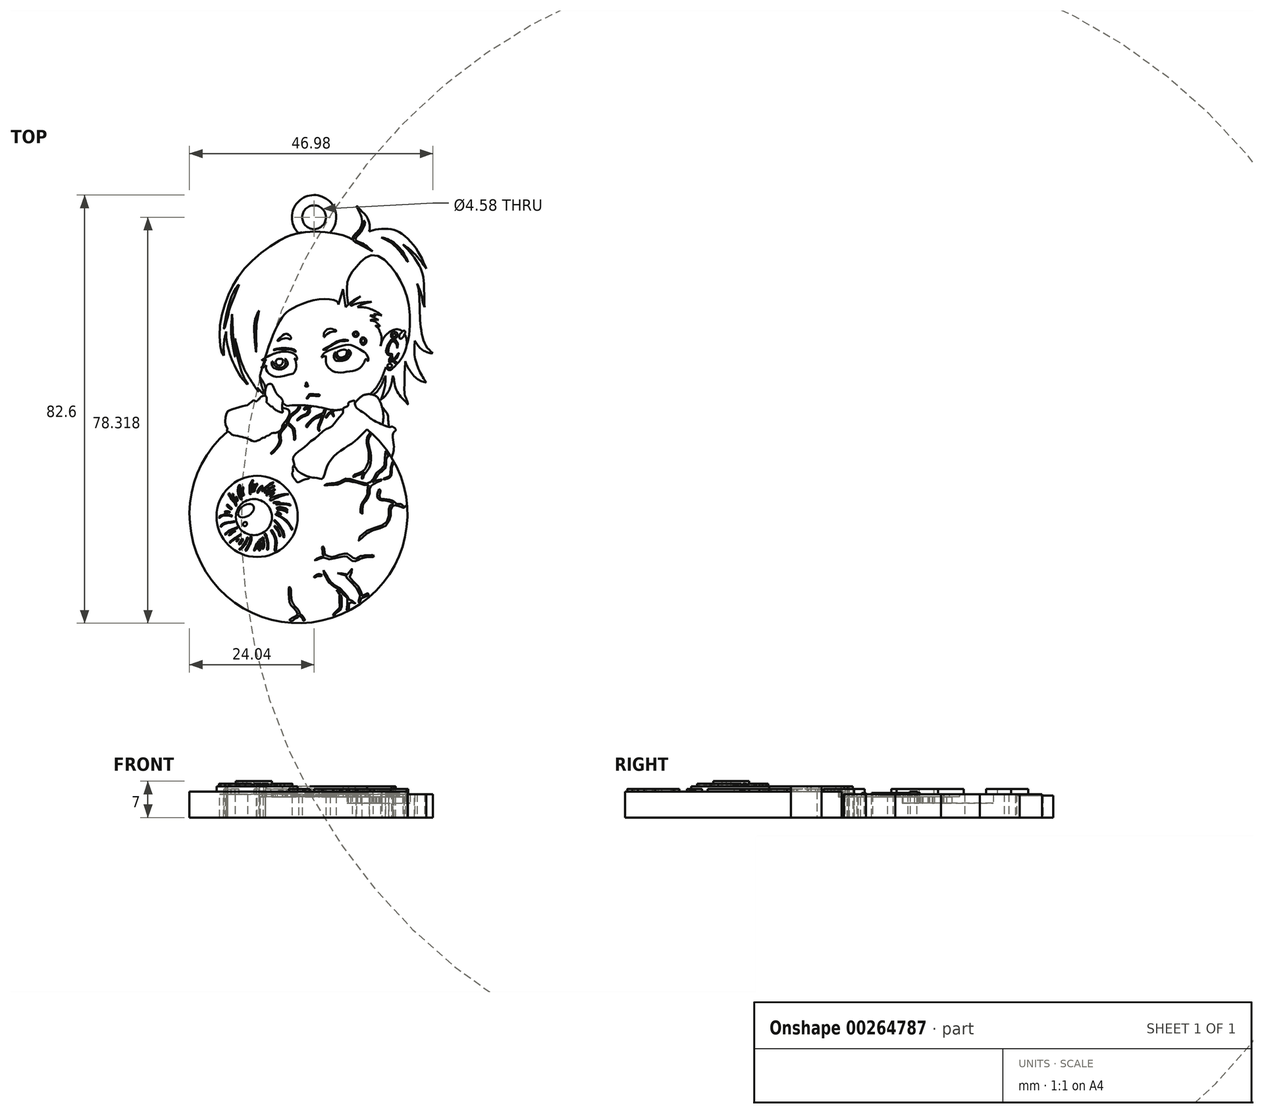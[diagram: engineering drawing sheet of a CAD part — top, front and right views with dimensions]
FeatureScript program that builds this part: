
annotation { "Feature Type Name" : "Feature", "Feature Type Description" : "" }
export const myFeature = defineFeature(function(context is Context, id is Id, definition is map)
    precondition{}
    {
        {
            var Q0;
            Q0=qCreatedBy(makeId("Top.planeOp"),FACE);
            var sketch = newSketch(context, id + "F0", { "sketchPlane" : qUnion([Q0])});
            skLineSegment(sketch, "E0", {"start": v(0, -34.76) * mm, "end": v(0, 40.24) * mm, "construction": true});
            skCircle(sketch, "E1", {"center": v(-3, -13.34) * mm, "radius": 21.03 * mm});
            skCircle(sketch, "E2", {"center": v(-10.98, -13.78) * mm, "radius": 7.83 * mm});
            skCircle(sketch, "E3", {"center": v(-11.61, -13.92) * mm, "radius": 3.48 * mm});
            skEllipse(sketch, "E4", {"center": v(-13.11, -12.67) * mm, "majorRadius": 1.7 * mm, "minorRadius": 1.07 * mm, "majorAxis": v(0.82, 0.58)});
            skEllipse(sketch, "E5", {"center": v(-13.33, -15.26) * mm, "majorRadius": 0.42 * mm, "minorRadius": 0.37 * mm, "majorAxis": v(0.66, 0.75)});
            skFitSpline(sketch, "E6", {"points": [v(5.58, 30.11) * mm, v(4.68, 27.12) * mm], "startDerivative": vector(-0.9, -3) * mm, "endDerivative": vector(-0.9, -3) * mm});
            skFitSpline(sketch, "E7", {"points": [v(4.68, 27.12) * mm, v(4.48, 27.66) * mm, v(0.94, 28.09) * mm, v(-4.3, 26.3) * mm, v(-6.06, 24.76) * mm, v(-8.26, 20.35) * mm, v(-10.45, 13.34) * mm], "startDerivative": vector(-0.38, 8.67) * mm, "endDerivative": vector(-8.55, -30.7) * mm});
            skFitSpline(sketch, "E8", {"points": [v(-10.45, 13.34) * mm, v(-9.57, 10.69) * mm, v(-5.18, 7.57) * mm, v(-5.04, 7.59) * mm], "startDerivative": vector(0.18, -6.54) * mm, "endDerivative": vector(0.96, 0.67) * mm, "construction": true});
            skFitSpline(sketch, "E9", {"points": [v(5.58, 30.11) * mm, v(6.1, 26.6) * mm], "startDerivative": vector(0.52, -3.51) * mm, "endDerivative": vector(0.52, -3.51) * mm});
            skFitSpline(sketch, "E10", {"points": [v(6.1, 26.6) * mm, v(7.25, 27.65) * mm, v(8.97, 28.67) * mm], "startDerivative": vector(2.26, 2.3) * mm, "endDerivative": vector(3.45, 1.84) * mm});
            skFitSpline(sketch, "E11", {"points": [v(8.97, 28.67) * mm, v(7.37, 27.4) * mm, v(7.02, 26.82) * mm], "startDerivative": vector(-3, -2.14) * mm, "endDerivative": vector(-0.67, -1.5) * mm});
            skFitSpline(sketch, "E12", {"points": [v(7.02, 26.82) * mm, v(8.36, 27.32) * mm, v(11.11, 27.65) * mm], "startDerivative": vector(2.88, 1.33) * mm, "endDerivative": vector(5.18, 0.37) * mm});
            skFitSpline(sketch, "E13", {"points": [v(11.11, 27.65) * mm, v(9.22, 27.12) * mm, v(8.36, 26.6) * mm], "startDerivative": vector(-3.6, -0.8) * mm, "endDerivative": vector(-1.81, -1.33) * mm});
            skFitSpline(sketch, "E14", {"points": [v(8.36, 26.6) * mm, v(10.24, 26.46) * mm, v(12.26, 25.6) * mm, v(13.1, 25) * mm], "startDerivative": vector(5.16, 0.08) * mm, "endDerivative": vector(2.75, -2.21) * mm});
            skFitSpline(sketch, "E15", {"points": [v(13.1, 25) * mm, v(12.29, 25.18) * mm, v(11.49, 25.26) * mm], "startDerivative": vector(-1.61, 0.44) * mm, "endDerivative": vector(-1.62, 0.1) * mm});
            skFitSpline(sketch, "E16", {"points": [v(11.49, 25.26) * mm, v(11.84, 24.84) * mm], "startDerivative": vector(0.36, -0.42) * mm, "endDerivative": vector(0.36, -0.42) * mm});
            skFitSpline(sketch, "E17", {"points": [v(11.84, 24.84) * mm, v(11.32, 24.98) * mm, v(10.77, 24.98) * mm], "startDerivative": vector(-1.03, 0.35) * mm, "endDerivative": vector(-1.1, -0.07) * mm});
            skFitSpline(sketch, "E18", {"points": [v(10.77, 24.98) * mm, v(11.49, 24.63) * mm, v(12.05, 24.34) * mm], "startDerivative": vector(1.4, -0.66) * mm, "endDerivative": vector(1.15, -0.62) * mm});
            skFitSpline(sketch, "E19", {"points": [v(12.05, 24.2) * mm, v(11.11, 24.18) * mm, v(10.77, 24.03) * mm], "startDerivative": vector(-1.72, 0.09) * mm, "endDerivative": vector(-0.75, -0.45) * mm});
            skFitSpline(sketch, "E20", {"points": [v(10.77, 24.03) * mm, v(11.72, 23.85) * mm, v(12.73, 22.94) * mm], "startDerivative": vector(2.12, -0.1) * mm, "endDerivative": vector(1.8, -2.01) * mm});
            skFitSpline(sketch, "E21", {"points": [v(12.73, 22.94) * mm, v(12.27, 22.94) * mm, v(11.84, 23.08) * mm], "startDerivative": vector(-0.93, -0.07) * mm, "endDerivative": vector(-0.85, 0.33) * mm});
            skFitSpline(sketch, "E22", {"points": [v(11.84, 23.08) * mm, v(12.05, 22.81) * mm, v(12.43, 22.56) * mm], "startDerivative": vector(0.39, -0.6) * mm, "endDerivative": vector(0.79, -0.44) * mm});
            skFitSpline(sketch, "E23", {"points": [v(12.43, 22.56) * mm, v(12.73, 21.82) * mm, v(13.03, 20.69) * mm, v(12.8, 19.08) * mm], "startDerivative": vector(1.04, -2.57) * mm, "endDerivative": vector(-1, -4.25) * mm});
            skFitSpline(sketch, "E24", {"points": [v(12.8, 19.08) * mm, v(13.4, 20.6) * mm, v(14.78, 21.94) * mm, v(16.64, 22.21) * mm, v(17.85, 20.34) * mm, v(17.08, 17.09) * mm, v(15.2, 14.82) * mm, v(14.61, 14.47) * mm, v(14.16, 14.62) * mm, v(13.86, 15.02) * mm], "startDerivative": vector(3.97, 13.82) * mm, "endDerivative": vector(-4.09, 7.1) * mm});
            skFitSpline(sketch, "E25", {"points": [v(13.86, 15.02) * mm, v(12.73, 12.26) * mm, v(10.77, 9.8) * mm, v(5.58, 6.93) * mm, v(2.97, 6.82) * mm], "startDerivative": vector(-4.59, -12.56) * mm, "endDerivative": vector(-10.9, 1.16) * mm});
            skFitSpline(sketch, "E26", {"points": [v(-10.45, 13.34) * mm, v(-10.16, 11.62) * mm, v(-9.57, 10.69) * mm, v(-5.3, 7.56) * mm], "startDerivative": vector(0.84, -6.71) * mm, "endDerivative": vector(10.7, -7.31) * mm});
            skFitSpline(sketch, "E27", {"points": [v(-5.3, 7.56) * mm, v(-3.07, 7.08) * mm, v(2.97, 6.82) * mm], "startDerivative": vector(5.13, -1.43) * mm, "endDerivative": vector(10.95, -0.15) * mm});
            skFitSpline(sketch, "E28", {"points": [v(12.05, 24.2) * mm, v(12.47, 24.09) * mm], "startDerivative": vector(0.42, -0.1) * mm, "endDerivative": vector(0.42, -0.1) * mm});
            skFitSpline(sketch, "E29", {"points": [v(12.05, 24.34) * mm, v(12.47, 24.09) * mm], "startDerivative": vector(0.42, -0.25) * mm, "endDerivative": vector(0.42, -0.25) * mm});
            skFitSpline(sketch, "E30", {"points": [v(-10.42, 13.07) * mm, v(-10.02, 12.46) * mm, v(-9.54, 11.58) * mm, v(-9.41, 10.76) * mm, v(-9.57, 10.4) * mm], "startDerivative": vector(1.55, -2.28) * mm, "endDerivative": vector(-1.1, -1.74) * mm});
            skFitSpline(sketch, "E31", {"points": [v(-9.57, 10.4) * mm, v(-9.57, 11.1) * mm, v(-10.02, 11.81) * mm, v(-10.26, 12.02) * mm], "startDerivative": vector(0.3, 1.92) * mm, "endDerivative": vector(-0.9, 0.65) * mm});
            skFitSpline(sketch, "E32", {"points": [v(-10.26, 12.02) * mm, v(-10.06, 11.22) * mm, v(-9.8, 10.55) * mm, v(-9.76, 9.84) * mm], "startDerivative": vector(0.48, -2.36) * mm, "endDerivative": vector(-0.04, -2.24) * mm});
            skFitSpline(sketch, "E33", {"points": [v(-9.76, 9.84) * mm, v(-10.26, 10.33) * mm, v(-10.96, 11.05) * mm], "startDerivative": vector(-1.04, 1.02) * mm, "endDerivative": vector(-1.34, 1.38) * mm});
            skFitSpline(sketch, "E34", {"points": [v(-10.96, 11.05) * mm, v(-10.82, 10.69) * mm, v(-10.68, 10.28) * mm], "startDerivative": vector(0.3, -0.72) * mm, "endDerivative": vector(0.25, -0.81) * mm});
            skFitSpline(sketch, "E35", {"points": [v(-10.68, 10.28) * mm, v(-11.1, 10.76) * mm, v(-12.08, 12.3) * mm, v(-13.34, 14.38) * mm, v(-14.31, 16.92) * mm, v(-15, 19.4) * mm, v(-15.26, 20.58) * mm], "startDerivative": vector(-3.85, 4.06) * mm, "endDerivative": vector(-1.7, 7.84) * mm});
            skFitSpline(sketch, "E36", {"points": [v(-15.26, 20.58) * mm, v(-14.82, 17.19) * mm, v(-14.06, 14.43) * mm, v(-13.38, 12.75) * mm, v(-12.93, 12.07) * mm, v(-12.82, 11.68) * mm], "startDerivative": vector(1.14, -12.13) * mm, "endDerivative": vector(0.06, -4.82) * mm});
            skFitSpline(sketch, "E37", {"points": [v(-12.82, 11.68) * mm, v(-13.67, 12.58) * mm, v(-15.47, 15.57) * mm, v(-16.5, 18.41) * mm, v(-16.9, 20.4) * mm, v(-16.95, 21.87) * mm], "startDerivative": vector(-5.16, 4.82) * mm, "endDerivative": vector(0.07, 8.66) * mm});
            skFitSpline(sketch, "E38", {"points": [v(-16.95, 21.87) * mm, v(-17.4, 19.73) * mm, v(-17.4, 17.29) * mm], "startDerivative": vector(-1.13, -4.32) * mm, "endDerivative": vector(0.23, -4.84) * mm});
            skFitSpline(sketch, "E39", {"points": [v(-17.4, 17.29) * mm, v(-17.91, 18.21) * mm, v(-18.13, 23.19) * mm, v(-16.37, 29.33) * mm, v(-13.15, 34.33) * mm, v(-7.4, 39.04) * mm, v(-3, 40.9) * mm, v(2.6, 41.04) * mm, v(6.38, 40.2) * mm, v(7.36, 39.66) * mm], "startDerivative": vector(-10.15, 12.6) * mm, "endDerivative": vector(14.26, -9.35) * mm});
            skFitSpline(sketch, "E40", {"points": [v(6.6, 27.1) * mm, v(6.43, 28.26) * mm, v(6.33, 30.55) * mm, v(6.8, 32.52) * mm, v(8.14, 34.36) * mm, v(9.76, 36.02) * mm, v(12.05, 36.6) * mm, v(15.18, 34.02) * mm, v(17.25, 30.46) * mm, v(18.46, 25.7) * mm, v(18.22, 20.5) * mm, v(17.85, 19.21) * mm], "startDerivative": vector(-3.09, 17.78) * mm, "endDerivative": vector(-6.02, -16.42) * mm});
            skFitSpline(sketch, "E41", {"points": [v(7.36, 39.66) * mm, v(7.63, 40.38) * mm, v(8.53, 41.33) * mm, v(9.18, 42.46) * mm, v(9.2, 43.8) * mm, v(8.45, 45.56) * mm, v(8.17, 45.94) * mm], "startDerivative": vector(1.2, 5.27) * mm, "endDerivative": vector(-2.32, 2.66) * mm});
            skFitSpline(sketch, "E42", {"points": [v(8.17, 45.94) * mm, v(8.17, 46.01) * mm, v(8.26, 46.07) * mm, v(9.14, 45.18) * mm, v(9.84, 44.48) * mm, v(10.47, 43.44) * mm, v(10.76, 42.12) * mm, v(10.62, 41.17) * mm], "startDerivative": vector(-0.3, 1.56) * mm, "endDerivative": vector(-1.33, -5.49) * mm});
            skFitSpline(sketch, "E43", {"points": [v(10.62, 41.17) * mm, v(12.06, 41.61) * mm, v(14.76, 41.64) * mm, v(16.97, 40.74) * mm, v(19.96, 37.49) * mm, v(21.65, 34.02) * mm], "startDerivative": vector(8.87, 3.5) * mm, "endDerivative": vector(6, -14.88) * mm});
            skFitSpline(sketch, "E44", {"points": [v(21.65, 34.02) * mm, v(19.22, 37.07) * mm, v(17.13, 38.73) * mm], "startDerivative": vector(-4.4, 6.1) * mm, "endDerivative": vector(-4.66, 3.22) * mm});
            skFitSpline(sketch, "E45", {"points": [v(17.13, 38.73) * mm, v(18.22, 37.57) * mm, v(19.68, 35.64) * mm, v(20.91, 33.13) * mm, v(21.23, 30.02) * mm, v(21.31, 26.57) * mm], "startDerivative": vector(6.89, -6.9) * mm, "endDerivative": vector(0.35, -15.15) * mm});
            skFitSpline(sketch, "E46", {"points": [v(21.31, 26.57) * mm, v(20.95, 27.65) * mm, v(20.75, 28.94) * mm, v(19.88, 31.15) * mm], "startDerivative": vector(-1.5, 3.74) * mm, "endDerivative": vector(-2.63, 5.69) * mm});
            skFitSpline(sketch, "E47", {"points": [v(19.88, 31.15) * mm, v(20.26, 29.29) * mm, v(20.4, 25.3) * mm, v(20.74, 21.75) * mm, v(21.65, 19.05) * mm, v(22.94, 17.75) * mm], "startDerivative": vector(2.72, -10) * mm, "endDerivative": vector(8.56, -6.83) * mm});
            skFitSpline(sketch, "E48", {"points": [v(22.94, 17.75) * mm, v(22.4, 17.75) * mm, v(20.76, 18.46) * mm, v(19.46, 20.14) * mm], "startDerivative": vector(-2.22, -0.26) * mm, "endDerivative": vector(-2.67, 4.52) * mm});
            skFitSpline(sketch, "E49", {"points": [v(19.46, 20.14) * mm, v(19.46, 16.97) * mm, v(20.52, 13.93) * mm, v(21.65, 12.06) * mm], "startDerivative": vector(-0.74, -8.97) * mm, "endDerivative": vector(3.88, -5.9) * mm});
            skFitSpline(sketch, "E50", {"points": [v(21.65, 12.06) * mm, v(19.88, 12.77) * mm, v(18.19, 14.85) * mm, v(17.6, 16.19) * mm], "startDerivative": vector(-5.45, 1.3) * mm, "endDerivative": vector(-0.83, 4.43) * mm});
            skFitSpline(sketch, "E51", {"points": [v(17.6, 16.19) * mm, v(17.45, 12.06) * mm, v(17.55, 9.48) * mm, v(18.02, 8.37) * mm, v(18.07, 7.84) * mm, v(17.95, 7.99) * mm], "startDerivative": vector(-1.15, -12.43) * mm, "endDerivative": vector(-3.15, 1.58) * mm});
            skFitSpline(sketch, "E52", {"points": [v(17.95, 7.99) * mm, v(17.6, 8.44) * mm, v(17.2, 8.8) * mm, v(15.84, 10.72) * mm, v(15.38, 12.83) * mm, v(15.2, 13.37) * mm], "startDerivative": vector(-1.6, 3.14) * mm, "endDerivative": vector(-1.32, 3.11) * mm});
            skFitSpline(sketch, "E53", {"points": [v(15.2, 13.37) * mm, v(14.75, 11.25) * mm, v(13.9, 9.68) * mm, v(12.81, 8.68) * mm], "startDerivative": vector(-0.97, -5.97) * mm, "endDerivative": vector(-3.83, -2.99) * mm});
            skFitSpline(sketch, "E54", {"points": [v(12.81, 8.68) * mm, v(13.23, 9.64) * mm, v(13.73, 11.8) * mm, v(13.77, 13.37) * mm], "startDerivative": vector(1.53, 3.05) * mm, "endDerivative": vector(-0.14, 4.4) * mm});
            skFitSpline(sketch, "E55", {"points": [v(13.77, 13.37) * mm, v(12.81, 11.27) * mm, v(11.54, 9.8) * mm, v(10.27, 9.4) * mm], "startDerivative": vector(-2.3, -5.76) * mm, "endDerivative": vector(-4.58, -0.8) * mm});
            skFitSpline(sketch, "E56", {"points": [v(-8.58, 11.81) * mm, v(-9.14, 11.44) * mm, v(-9.41, 9.56) * mm, v(-9.2, 9.26) * mm, v(-9.15, 8.51) * mm, v(-9.2, 8.32) * mm, v(-8.74, 7.85) * mm, v(-8.24, 7.4) * mm, v(-8, 7.39) * mm, v(-7.75, 7.03) * mm, v(-6.2, 6.3) * mm, v(-6.01, 6.4) * mm, v(-6.1, 6.72) * mm, v(-6.13, 7.85) * mm, v(-6.03, 8.51) * mm, v(-6.55, 9.27) * mm, v(-7.23, 9.9) * mm, v(-7.74, 10.95) * mm, v(-8.14, 11.7) * mm, v(-8.58, 11.81) * mm]});
            skFitSpline(sketch, "E57", {"points": [v(-9.41, 9.56) * mm, v(-10.1, 9.38) * mm, v(-10.51, 9.06) * mm, v(-10.54, 8.83) * mm], "startDerivative": vector(-1.78, -0.33) * mm, "endDerivative": vector(-0.03, -1.55) * mm});
            skFitSpline(sketch, "E58", {"points": [v(-10.54, 8.83) * mm, v(-10.7, 8.83) * mm, v(-10.93, 8.56) * mm, v(-11.16, 8.4) * mm], "startDerivative": vector(-1.15, 0.03) * mm, "endDerivative": vector(-0.57, -0.65) * mm});
            skFitSpline(sketch, "E59", {"points": [v(-11.16, 8.4) * mm, v(-11.4, 8.53) * mm, v(-11.7, 8.62) * mm, v(-11.94, 8.4) * mm, v(-12.28, 8.15) * mm, v(-12.48, 7.98) * mm, v(-12.8, 7.73) * mm, v(-13.88, 7.45) * mm, v(-16, 6.83) * mm, v(-16.83, 6.28) * mm, v(-17.01, 3.73) * mm, v(-16.71, 3.09) * mm, v(-16.81, 2.73) * mm, v(-16.2, 2.35) * mm, v(-15.96, 2.07) * mm, v(-14.06, 1.61) * mm, v(-12.53, 1.1) * mm, v(-11.43, 0.7) * mm, v(-9.78, 1.45) * mm], "startDerivative": vector(-7.25, 5.43) * mm, "endDerivative": vector(21.54, 13.84) * mm});
            skFitSpline(sketch, "E60", {"points": [v(-9.78, 1.45) * mm, v(-9.53, 1.4) * mm, v(-9.29, 1.67) * mm, v(-8.72, 1.86) * mm, v(-8.22, 2.26) * mm, v(-7.45, 2.35) * mm, v(-6.35, 2.98) * mm, v(-6.1, 3.86) * mm, v(-5.17, 5.05) * mm, v(-4.73, 6.4) * mm, v(-5.08, 6.9) * mm, v(-5.48, 7.03) * mm, v(-6.16, 7.2) * mm], "startDerivative": vector(5.46, -2.61) * mm, "endDerivative": vector(-8.94, 2.33) * mm});
            skFitSpline(sketch, "E61", {"points": [v(7.9, 7.9) * mm, v(7.8, 8.52) * mm, v(7.2, 8.44) * mm, v(6.66, 8.19) * mm, v(6.6, 7.64) * mm, v(6.04, 7.31) * mm, v(5.63, 7.08) * mm, v(5.58, 6.26) * mm, v(4.52, 5) * mm, v(3.35, 3.5) * mm, v(3.1, 3.47) * mm, v(2.86, 3.24) * mm, v(2.38, 3.1) * mm, v(-0.08, 1.06) * mm, v(-0.64, 0.76) * mm, v(-1.38, 0) * mm, v(-2.73, -1.03) * mm, v(-4.06, -2.46) * mm, v(-3.91, -3.3) * mm, v(-3.76, -4.15) * mm, v(-3.57, -4.4) * mm, v(-2.98, -5.12) * mm, v(-0.62, -6.24) * mm, v(0.11, -6.3) * mm, v(1.05, -6.5) * mm, v(1.66, -6.47) * mm, v(2.24, -4.84) * mm, v(3.42, -2.64) * mm, v(5.58, -0.79) * mm, v(7.76, 0.66) * mm, v(9.3, 2.09) * mm, v(10.21, 3.01) * mm], "startDerivative": vector(0.5, 33.2) * mm, "endDerivative": vector(24.67, 24.62) * mm});
            skFitSpline(sketch, "E62", {"points": [v(7.9, 7.9) * mm, v(8.28, 7.12) * mm, v(9.8, 6.08) * mm, v(10.94, 5.09) * mm, v(12.73, 4.13) * mm, v(14.56, 3.5) * mm, v(15.26, 3.5) * mm, v(15.75, 2.88) * mm, v(15.26, 2.3) * mm, v(15.38, 0) * mm, v(15.26, -1.48) * mm, v(14.95, -2.4) * mm], "startDerivative": vector(2.9, -10.88) * mm, "endDerivative": vector(-4.44, -11.55) * mm});
            skFitSpline(sketch, "E63", {"points": [v(7.9, 8.07) * mm, v(8.23, 8.54) * mm, v(9.13, 9.37) * mm, v(10.37, 9.8) * mm, v(12, 9.4) * mm, v(12.93, 7.9) * mm, v(13.38, 5.69) * mm, v(13.21, 3.92) * mm], "startDerivative": vector(3.02, 4.9) * mm, "endDerivative": vector(-1.87, -10.83) * mm});
            skFitSpline(sketch, "E64", {"points": [v(13.1, 7.35) * mm, v(13.9, 6.39) * mm, v(14.25, 5.69) * mm, v(14.33, 4.5) * mm, v(14.44, 3.65) * mm, v(14.43, 3.5) * mm], "startDerivative": vector(3.42, -3.98) * mm, "endDerivative": vector(-0.27, -1.3) * mm});
            skFitSpline(sketch, "E65", {"points": [v(-3.84, -3.75) * mm, v(-4.1, -4.4) * mm, v(-4.09, -5.07) * mm, v(-4.22, -5.4) * mm, v(-4.04, -6.18) * mm, v(-3.57, -6.78) * mm, v(-3.21, -7.2) * mm, v(-2.14, -6.77) * mm, v(-1.02, -6.43) * mm, v(-0.8, -6.2) * mm], "startDerivative": vector(-3.24, -5.47) * mm, "endDerivative": vector(1.96, 3.52) * mm});
            skSolve(sketch);
        }
        {
            var Q0;
            Q0=makeQuery(id+"F0.imprint","IMPRINT",FACE,{"disambiguationData":[TD([[makeQuery(id+"F0.imprint","IMPRINT",EDGE,{"derivedFrom":sQuery(id+"F0.wireOp",EDGE,"E2")}),-1.0]])]});
            var Q1;
            {var subQ0=sQuery(id+"F0.wireOp",EDGE,"E27");Q1=makeQuery(id+"F0.imprint","IMPRINT",FACE,{"disambiguationData":[TD([[makeQuery(id+"F0.imprint","IMPRINT",EDGE,{"derivedFrom":subQ0}),1.0]])]});}
            extrude(context, id + "F1", {"entities" : qUnion([Q0, Q1]), "depth" : 5 * mm, "offsetDistance" : 25 * mm});
        }
        {
            var Q0;
            Q0=makeQuery(id+"F0.imprint","IMPRINT",FACE,{"disambiguationData":[TD([[makeQuery(id+"F0.imprint","IMPRINT",EDGE,{"derivedFrom":sQuery(id+"F0.wireOp",EDGE,"E2")}),1.0]])]});
            extrude(context, id + "F2", {"entities" : qUnion([Q0]), "operationType" : NewBodyOperationType.ADD, "depth" : 6 * mm, "offsetDistance" : 25 * mm});
        }
        {
            var Q0;
            Q0=makeQuery(id+"F0.imprint","IMPRINT",FACE,{"disambiguationData":[TD([[makeQuery(id+"F0.imprint","IMPRINT",EDGE,{"derivedFrom":sQuery(id+"F0.wireOp",EDGE,"E3")}),1.0]])]});
            extrude(context, id + "F3", {"entities" : qUnion([Q0]), "operationType" : NewBodyOperationType.ADD, "depth" : 7 * mm, "offsetDistance" : 25 * mm});
        }
        {
            var Q0;
            Q0=makeQuery(id+"F0.imprint","IMPRINT",FACE,{"disambiguationData":[TD([[makeQuery(id+"F0.imprint","IMPRINT",EDGE,{"derivedFrom":sQuery(id+"F0.wireOp",EDGE,"E4")}),1.0]])]});
            var Q1;
            Q1=makeQuery(id+"F0.imprint","IMPRINT",FACE,{"disambiguationData":[TD([[makeQuery(id+"F0.imprint","IMPRINT",EDGE,{"derivedFrom":sQuery(id+"F0.wireOp",EDGE,"E5")}),1.0]])]});
            extrude(context, id + "F4", {"entities" : qUnion([Q0, Q1]), "operationType" : NewBodyOperationType.ADD, "depth" : 6 * mm, "offsetDistance" : 25 * mm});
        }
        {
            var Q0;
            Q0=makeQuery(id+"F0.imprint","IMPRINT",FACE,{"disambiguationData":[TD([[makeQuery(id+"F0.imprint","IMPRINT",EDGE,{"derivedFrom":sQuery(id+"F0.wireOp",EDGE,"E6")}),1.0]])]});
            extrude(context, id + "F5", {"entities" : qUnion([Q0]), "operationType" : NewBodyOperationType.ADD, "depth" : 4 * mm, "offsetDistance" : 25 * mm});
        }
        {
            var Q0;
            Q0=makeQuery(id+"F0.imprint","IMPRINT",FACE,{"disambiguationData":[TD([[makeQuery(id+"F0.imprint","IMPRINT",EDGE,{"derivedFrom":sQuery(id+"F0.wireOp",EDGE,"E6")}),-1.0]])]});
            extrude(context, id + "F6", {"entities" : qUnion([Q0]), "operationType" : NewBodyOperationType.ADD, "depth" : 4.5 * mm, "offsetDistance" : 25 * mm});
        }
        {
            var Q0;
            {var subQ0=sQuery(id+"F0.wireOp",EDGE,"E11");Q0=makeQuery(id+"F0.imprint","IMPRINT",FACE,{"disambiguationData":[TD([[makeQuery(id+"F0.imprint","IMPRINT",EDGE,{"derivedFrom":subQ0}),1.0]])]});}
            extrude(context, id + "F7", {"entities" : qUnion([Q0]), "operationType" : NewBodyOperationType.ADD, "depth" : 2.75 * mm, "offsetDistance" : 25 * mm});
        }
        {
            var Q0;
            {var subQ0=sQuery(id+"F0.wireOp",EDGE,"E56");var subQ1=sQuery(id+"F0.wireOp",EDGE,"E26");var subQ2=makeQuery(id+"F0.imprint","INTERSECT",VERTEX,{"disambiguationData":[OD(0.0)],"derivedFrom":[subQ1,subQ0]});Q0=makeQuery(id+"F0.imprint","IMPRINT",FACE,{"disambiguationData":[TD([[makeQuery(id+"F0.imprint","IMPRINT",EDGE,{"disambiguationData":[TD([[subQ2,-1.0]])],"derivedFrom":subQ1}),1.0]])]});}
            var Q1;
            {var subQ0=sQuery(id+"F0.wireOp",EDGE,"E56");var subQ4=sQuery(id+"F0.wireOp",EDGE,"E1");var subQ7=makeQuery(id+"F0.imprint","INTERSECT",VERTEX,{"disambiguationData":[OD(0.0)],"derivedFrom":[subQ4,subQ0]});Q1=makeQuery(id+"F0.imprint","IMPRINT",FACE,{"disambiguationData":[TD([[makeQuery(id+"F0.imprint","IMPRINT",EDGE,{"disambiguationData":[TD([[subQ7,-1.0]])],"derivedFrom":subQ4}),-1.0]])]});}
            var Q2;
            {var subQ0=sQuery(id+"F0.wireOp",EDGE,"E56");var subQ1=sQuery(id+"F0.wireOp",EDGE,"E1");var subQ2=makeQuery(id+"F0.imprint","INTERSECT",VERTEX,{"disambiguationData":[OD(0.0)],"derivedFrom":[subQ1,subQ0]});Q2=makeQuery(id+"F0.imprint","IMPRINT",FACE,{"disambiguationData":[TD([[makeQuery(id+"F0.imprint","IMPRINT",EDGE,{"disambiguationData":[TD([[subQ2,-1.0]])],"derivedFrom":subQ1}),1.0]])]});}
            var Q3;
            {var subQ2=sQuery(id+"F0.wireOp",EDGE,"E55");var subQ5=sQuery(id+"F0.wireOp",EDGE,"E25");var subQ8=makeQuery(id+"F0.imprint","INTERSECT",VERTEX,{"derivedFrom":[subQ5,subQ2]});Q3=makeQuery(id+"F0.imprint","IMPRINT",FACE,{"disambiguationData":[TD([[makeQuery(id+"F0.imprint","IMPRINT",EDGE,{"disambiguationData":[TD([[subQ8,1.0]])],"derivedFrom":subQ2}),1.0]])]});}
            var Q4;
            {var subQ0=sQuery(id+"F0.wireOp",EDGE,"E25");var subQ1=makeQuery(id+"F0.imprint","INTERSECT",VERTEX,{"derivedFrom":[subQ0,sQuery(id+"F0.wireOp",EDGE,"E55")]});Q4=makeQuery(id+"F0.imprint","IMPRINT",FACE,{"disambiguationData":[TD([[makeQuery(id+"F0.imprint","IMPRINT",EDGE,{"disambiguationData":[TD([[subQ1,1.0]])],"derivedFrom":subQ0}),-1.0]])]});}
            var Q5;
            {var subQ0=sQuery(id+"F0.wireOp",EDGE,"E55");var subQ1=sQuery(id+"F0.wireOp",EDGE,"E25");var subQ2=makeQuery(id+"F0.imprint","INTERSECT",VERTEX,{"derivedFrom":[subQ1,subQ0]});Q5=makeQuery(id+"F0.imprint","IMPRINT",FACE,{"disambiguationData":[TD([[makeQuery(id+"F0.imprint","IMPRINT",EDGE,{"disambiguationData":[TD([[subQ2,1.0]])],"derivedFrom":subQ1}),1.0]])]});}
            var Q6;
            {var subQ0=sQuery(id+"F0.wireOp",EDGE,"E65");Q6=makeQuery(id+"F0.imprint","IMPRINT",FACE,{"disambiguationData":[TD([[makeQuery(id+"F0.imprint","IMPRINT",EDGE,{"derivedFrom":subQ0}),1.0]])]});}
            extrude(context, id + "F8", {"entities" : qUnion([Q0, Q1, Q2, Q3, Q4, Q5, Q6]), "operationType" : NewBodyOperationType.ADD, "depth" : 5.5 * mm, "offsetDistance" : 25 * mm});
        }
        {
            var Q0;
            {var subQ1=sQuery(id+"F0.wireOp",EDGE,"E57");Q0=makeQuery(id+"F0.imprint","IMPRINT",FACE,{"disambiguationData":[TD([[makeQuery(id+"F0.imprint","IMPRINT",EDGE,{"derivedFrom":subQ1}),1.0]])]});}
            var Q1;
            {var subQ5=sQuery(id+"F0.wireOp",EDGE,"E60");Q1=makeQuery(id+"F0.imprint","IMPRINT",FACE,{"disambiguationData":[TD([[makeQuery(id+"F0.imprint","IMPRINT",EDGE,{"derivedFrom":subQ5}),1.0]])]});}
            var Q2;
            {var subQ0=sQuery(id+"F0.wireOp",EDGE,"E61");var subQ1=sQuery(id+"F0.wireOp",EDGE,"E1");var subQ2=makeQuery(id+"F0.imprint","INTERSECT",VERTEX,{"disambiguationData":[OD(0.0)],"derivedFrom":[subQ1,subQ0]});Q2=makeQuery(id+"F0.imprint","IMPRINT",FACE,{"disambiguationData":[TD([[makeQuery(id+"F0.imprint","IMPRINT",EDGE,{"disambiguationData":[TD([[subQ2,-1.0]])],"derivedFrom":subQ1}),1.0]])]});}
            var Q3;
            {var subQ0=sQuery(id+"F0.wireOp",EDGE,"E61");var subQ1=sQuery(id+"F0.wireOp",EDGE,"E1");var subQ2=makeQuery(id+"F0.imprint","INTERSECT",VERTEX,{"disambiguationData":[OD(0.0)],"derivedFrom":[subQ1,subQ0]});Q3=makeQuery(id+"F0.imprint","IMPRINT",FACE,{"disambiguationData":[TD([[makeQuery(id+"F0.imprint","IMPRINT",EDGE,{"disambiguationData":[TD([[subQ2,1.0]])],"derivedFrom":subQ1}),-1.0]])]});}
            var Q4;
            {var subQ0=sQuery(id+"F0.wireOp",EDGE,"E61");var subQ4=makeQuery(id+"F0.imprint","INTERSECT",VERTEX,{"derivedFrom":[subQ0,sQuery(id+"F0.wireOp",EDGE,"E63")]});Q4=makeQuery(id+"F0.imprint","IMPRINT",FACE,{"disambiguationData":[TD([[makeQuery(id+"F0.imprint","IMPRINT",EDGE,{"disambiguationData":[TD([[subQ4,-1.0]])],"derivedFrom":subQ0}),1.0]])]});}
            extrude(context, id + "F9", {"entities" : qUnion([Q0, Q1, Q2, Q3, Q4]), "operationType" : NewBodyOperationType.ADD, "depth" : 6 * mm, "offsetDistance" : 25 * mm});
        }
        {
            var Q0;
            {var subQ3=sQuery(id+"F0.wireOp",EDGE,"E64");Q0=makeQuery(id+"F0.imprint","IMPRINT",FACE,{"disambiguationData":[TD([[makeQuery(id+"F0.imprint","IMPRINT",EDGE,{"derivedFrom":subQ3}),-1.0]])]});}
            var Q1;
            {var subQ1=sQuery(id+"F0.wireOp",EDGE,"E1");var subQ3=sQuery(id+"F0.wireOp",EDGE,"E61");var subQ4=makeQuery(id+"F0.imprint","INTERSECT",VERTEX,{"disambiguationData":[OD(1.0)],"derivedFrom":[subQ1,subQ3]});Q1=makeQuery(id+"F0.imprint","IMPRINT",FACE,{"disambiguationData":[TD([[makeQuery(id+"F0.imprint","IMPRINT",EDGE,{"disambiguationData":[TD([[subQ4,1.0]])],"derivedFrom":subQ3}),-1.0]])]});}
            var Q2;
            {var subQ1=sQuery(id+"F0.wireOp",EDGE,"E1");var subQ3=sQuery(id+"F0.wireOp",EDGE,"E56");var subQ4=makeQuery(id+"F0.imprint","INTERSECT",VERTEX,{"disambiguationData":[OD(0.0)],"derivedFrom":[subQ1,subQ3]});Q2=makeQuery(id+"F0.imprint","IMPRINT",FACE,{"disambiguationData":[TD([[makeQuery(id+"F0.imprint","IMPRINT",EDGE,{"disambiguationData":[TD([[subQ4,-1.0]])],"derivedFrom":subQ3}),-1.0]])]});}
            extrude(context, id + "F10", {"entities" : qUnion([Q0, Q1, Q2]), "operationType" : NewBodyOperationType.ADD, "depth" : 5 * mm, "offsetDistance" : 25 * mm});
        }
        {
            var Q0;
            Q0=qCreatedBy(makeId("Top.planeOp"),FACE);
            var sketch = newSketch(context, id + "F11", { "sketchPlane" : qUnion([Q0])});
            skFitSpline(sketch, "E66", {"points": [v(1.47, 16.88) * mm, v(1.69, 17.46) * mm, v(2.62, 18.12) * mm, v(5.61, 19.22) * mm, v(7.43, 19.2) * mm, v(9.52, 18.02) * mm, v(10, 17.66) * mm, v(10.5, 16.59) * mm, v(10.35, 16.13) * mm], "startDerivative": vector(1.7, 6.98) * mm, "endDerivative": vector(-3.1, -5.02) * mm});
            skFitSpline(sketch, "E67", {"points": [v(1.47, 16.88) * mm, v(2.05, 17.14) * mm, v(2.28, 17.16) * mm], "startDerivative": vector(1.03, 0.53) * mm, "endDerivative": vector(0.57, -0.02) * mm});
            skFitSpline(sketch, "E68", {"points": [v(2.28, 17.16) * mm, v(2.28, 16.13) * mm, v(2.72, 15) * mm, v(4.34, 14.03) * mm, v(6.67, 14.17) * mm, v(8.6, 14.71) * mm, v(9.7, 16) * mm, v(9.88, 16.5) * mm], "startDerivative": vector(-0.5, -8.52) * mm, "endDerivative": vector(1.3, 5.03) * mm});
            skFitSpline(sketch, "E69", {"points": [v(9.88, 16.5) * mm, v(9.97, 16.59) * mm, v(10.17, 16.5) * mm, v(10.35, 16.13) * mm], "startDerivative": vector(0.33, 0.44) * mm, "endDerivative": vector(0.33, -0.99) * mm});
            skFitSpline(sketch, "E70", {"points": [v(-3.23, 16.59) * mm, v(-3.78, 17.55) * mm, v(-6.23, 17.99) * mm, v(-9.13, 16.98) * mm, v(-10.14, 16.33) * mm], "startDerivative": vector(-1.64, 4.96) * mm, "endDerivative": vector(-1.46, -1.38) * mm});
            skFitSpline(sketch, "E71", {"points": [v(-10.14, 16.33) * mm, v(-9.66, 16.42) * mm, v(-9.2, 16.54) * mm], "startDerivative": vector(0.95, 0.17) * mm, "endDerivative": vector(0.94, 0.25) * mm});
            skFitSpline(sketch, "E72", {"points": [v(-9.2, 16.54) * mm, v(-9.5, 16.04) * mm, v(-9.73, 15.45) * mm, v(-10.23, 14.9) * mm], "startDerivative": vector(-1.11, -1.51) * mm, "endDerivative": vector(-1.6, -1.48) * mm});
            skFitSpline(sketch, "E73", {"points": [v(-10.23, 14.9) * mm, v(-9.82, 14.96) * mm, v(-9.2, 15.41) * mm], "startDerivative": vector(0.94, 0.03) * mm, "endDerivative": vector(1.12, 0.96) * mm});
            skFitSpline(sketch, "E74", {"points": [v(-3.23, 16.59) * mm, v(-3.34, 16.46) * mm, v(-3.57, 16.59) * mm, v(-3.8, 16.68) * mm], "startDerivative": vector(-0.32, -0.62) * mm, "endDerivative": vector(-0.65, 0.2) * mm});
            skFitSpline(sketch, "E75", {"points": [v(-3.8, 16.68) * mm, v(-3.57, 16.3) * mm, v(-3.45, 15.4) * mm, v(-3.5, 14.58) * mm, v(-4.1, 13.77) * mm, v(-4.62, 13.63) * mm, v(-7.21, 13.16) * mm, v(-8.95, 14.07) * mm, v(-9.29, 14.71) * mm, v(-9.2, 15.41) * mm], "startDerivative": vector(3.52, -4.33) * mm, "endDerivative": vector(1.87, 7.74) * mm});
            skFitSpline(sketch, "E76", {"points": [v(-8.14, 16.1) * mm, v(-8.15, 15.58) * mm, v(-7.93, 15.04) * mm, v(-7.38, 14.7) * mm, v(-6.3, 14.6) * mm, v(-5.51, 15) * mm, v(-5.15, 15.4) * mm, v(-5.16, 16.1) * mm, v(-5.48, 16.59) * mm, v(-5.64, 16.59) * mm], "startDerivative": vector(-0.54, -4.97) * mm, "endDerivative": vector(-2.75, -0.75) * mm});
            skFitSpline(sketch, "E77", {"points": [v(-5.64, 16.59) * mm, v(-5.49, 16.07) * mm, v(-5.64, 15.34) * mm, v(-6.15, 14.98) * mm, v(-7.09, 14.98) * mm, v(-7.74, 15.6) * mm, v(-7.92, 16.1) * mm], "startDerivative": vector(1.41, -3.29) * mm, "endDerivative": vector(-0.8, 3.37) * mm});
            skFitSpline(sketch, "E78", {"points": [v(-7.92, 16.1) * mm, v(-8.14, 16.1) * mm], "startDerivative": vector(-0.23, 0) * mm, "endDerivative": vector(-0.23, 0) * mm});
            skFitSpline(sketch, "E79", {"points": [v(-7.24, 16.44) * mm, v(-7.38, 16.2) * mm, v(-7.39, 15.83) * mm, v(-7.12, 15.46) * mm, v(-6.57, 15.35) * mm, v(-6.1, 15.8) * mm, v(-6, 16.22) * mm, v(-6.13, 16.59) * mm, v(-6.7, 16.63) * mm, v(-7.1, 16.56) * mm, v(-7.24, 16.44) * mm]});
            skFitSpline(sketch, "E80", {"points": [v(4.43, 17.84) * mm, v(4.49, 17.43) * mm, v(4.85, 16.96) * mm, v(5.87, 17.07) * mm, v(6.32, 17.72) * mm, v(6.28, 18.23) * mm, v(5.97, 18.38) * mm, v(5.23, 18.3) * mm, v(4.55, 18.04) * mm, v(4.43, 17.84) * mm]});
            skFitSpline(sketch, "E81", {"points": [v(4.03, 17.82) * mm, v(3.84, 17.45) * mm, v(3.79, 16.98) * mm, v(4.14, 16.34) * mm, v(5.01, 16.22) * mm, v(5.92, 16.33) * mm, v(6.8, 17) * mm, v(7.08, 17.82) * mm, v(6.73, 18.34) * mm], "startDerivative": vector(-2.3, -3.8) * mm, "endDerivative": vector(-4.11, 4) * mm});
            skFitSpline(sketch, "E82", {"points": [v(4.03, 17.82) * mm, v(4.2, 17.87) * mm, v(4.15, 17.4) * mm, v(4.44, 16.75) * mm, v(5.45, 16.57) * mm, v(6.3, 16.98) * mm, v(6.63, 17.65) * mm, v(6.67, 18.13) * mm, v(6.62, 18.36) * mm, v(6.73, 18.34) * mm], "startDerivative": vector(3.1, 1.74) * mm, "endDerivative": vector(2.74, -1.13) * mm});
            skFitSpline(sketch, "E83", {"points": [v(-7.65, 18.47) * mm, v(-7.31, 18.58) * mm, v(-6.4, 18.7) * mm, v(-4.9, 18.69) * mm, v(-3.8, 18.38) * mm, v(-3.51, 18.07) * mm, v(-3.64, 17.97) * mm, v(-3.93, 18.2) * mm, v(-5.4, 18.45) * mm, v(-7.38, 18.36) * mm, v(-7.8, 18.29) * mm, v(-7.65, 18.47) * mm]});
            skFitSpline(sketch, "E84", {"points": [v(6.52, 20.27) * mm, v(5.34, 20.24) * mm, v(3.73, 19.58) * mm, v(2.13, 18.66) * mm, v(1.74, 18.4) * mm, v(2.03, 18.33) * mm, v(2.92, 18.89) * mm, v(4.25, 19.68) * mm, v(5.27, 20.05) * mm, v(6.51, 20.1) * mm, v(6.58, 20.15) * mm, v(6.57, 20.24) * mm, v(6.52, 20.27) * mm]});
            skFitSpline(sketch, "E85", {"points": [v(-5.73, 20.59) * mm, v(-4.94, 20.53) * mm, v(-4.62, 20.38) * mm, v(-4.44, 20.58) * mm, v(-4.66, 21.1) * mm, v(-5.24, 21.44) * mm, v(-5.74, 21.36) * mm, v(-6.46, 20.79) * mm, v(-7.02, 20.28) * mm, v(-7.04, 20.08) * mm, v(-6.8, 20.1) * mm, v(-6.55, 20.26) * mm, v(-6.22, 20.44) * mm, v(-5.73, 20.59) * mm]});
            skFitSpline(sketch, "E86", {"points": [v(1.92, 20.9) * mm, v(1.87, 21.23) * mm, v(2.05, 21.84) * mm, v(2.73, 22.4) * mm, v(3.63, 22.35) * mm, v(4.26, 22.1) * mm, v(4.21, 21.92) * mm, v(3.77, 21.88) * mm, v(2.94, 21.65) * mm, v(2.12, 21.02) * mm, v(2.03, 20.81) * mm, v(1.92, 20.9) * mm]});
            skFitSpline(sketch, "E87", {"points": [v(-1.43, 12.06) * mm, v(-1.56, 12.03) * mm, v(-1.63, 11.67) * mm, v(-1.73, 11.4) * mm, v(-1.5, 11.26) * mm, v(-1.17, 11.34) * mm, v(-1.23, 11.62) * mm, v(-1.34, 11.99) * mm, v(-1.43, 12.06) * mm]});
            skFitSpline(sketch, "E88", {"points": [v(-1.35, 8.91) * mm, v(-1.45, 9) * mm, v(-1.3, 9.26) * mm, v(-0.94, 9.77) * mm, v(-0.55, 9.83) * mm, v(0.86, 9.78) * mm, v(1.04, 9.73) * mm, v(1.08, 9.56) * mm, v(0.96, 9.47) * mm, v(0, 9.48) * mm, v(-0.74, 9.53) * mm, v(-1.04, 9.23) * mm, v(-1.35, 8.91) * mm]});
            skSolve(sketch);
        }
        {
            var Q0;
            Q0 = qSketchRegion(id + "F11", true);
            extrude(context, id + "F12", {"entities" : qUnion([Q0]), "operationType" : NewBodyOperationType.ADD, "depth" : 4.75 * mm, "offsetDistance" : 25 * mm});
        }
        {
            var Q0;
            Q0=qCreatedBy(makeId("Top.planeOp"),FACE);
            var sketch = newSketch(context, id + "F13", { "sketchPlane" : qUnion([Q0])});
            skFitSpline(sketch, "E89", {"points": [v(7.68, 21.8) * mm, v(7.53, 21.54) * mm, v(7.66, 20.98) * mm, v(8.14, 20.86) * mm, v(8.55, 21.2) * mm, v(8.45, 21.71) * mm, v(8, 21.9) * mm, v(7.68, 21.8) * mm]});
            skFitSpline(sketch, "E90", {"points": [v(7.8, 21.64) * mm, v(7.75, 21.4) * mm, v(7.83, 21.11) * mm, v(8.12, 21.09) * mm, v(8.35, 21.27) * mm, v(8.27, 21.58) * mm, v(8, 21.7) * mm, v(7.8, 21.64) * mm]});
            skFitSpline(sketch, "E91", {"points": [v(9.18, 20.66) * mm, v(9, 20.42) * mm, v(8.94, 20.03) * mm, v(9.06, 19.65) * mm, v(9.3, 19.34) * mm, v(9.72, 19.37) * mm, v(10.04, 19.77) * mm, v(10.07, 20.27) * mm, v(9.72, 20.73) * mm, v(9.32, 20.76) * mm, v(9.18, 20.66) * mm]});
            skFitSpline(sketch, "E92", {"points": [v(9.3, 20.5) * mm, v(9.18, 20.25) * mm, v(9.18, 19.9) * mm, v(9.39, 19.7) * mm, v(9.65, 19.76) * mm, v(9.81, 20.04) * mm, v(9.72, 20.4) * mm, v(9.4, 20.55) * mm, v(9.3, 20.5) * mm]});
            skFitSpline(sketch, "E93", {"points": [v(15.17, 21.83) * mm, v(14.88, 21.45) * mm, v(14.9, 20.85) * mm, v(15.36, 20.6) * mm, v(15.93, 20.75) * mm, v(16.1, 21.2) * mm, v(16, 21.65) * mm, v(15.54, 21.87) * mm, v(15.17, 21.83) * mm]});
            skFitSpline(sketch, "E94", {"points": [v(15.34, 21.5) * mm, v(15.19, 21.3) * mm, v(15.2, 20.98) * mm, v(15.57, 20.88) * mm, v(15.8, 21.2) * mm, v(15.66, 21.42) * mm, v(15.34, 21.5) * mm]});
            skFitSpline(sketch, "E95", {"points": [v(14.56, 15.67) * mm, v(14.25, 15.56) * mm, v(14.17, 15.22) * mm, v(14.43, 14.95) * mm, v(14.78, 14.94) * mm, v(15, 15.18) * mm, v(14.97, 15.55) * mm, v(14.56, 15.67) * mm]});
            skFitSpline(sketch, "E96", {"points": [v(15.7, 16.11) * mm, v(15.53, 15.98) * mm, v(15.63, 15.74) * mm, v(15.93, 15.87) * mm, v(15.7, 16.11) * mm]});
            skFitSpline(sketch, "E97", {"points": [v(16.1, 18.63) * mm, v(16.2, 19) * mm, v(16.11, 19.72) * mm, v(15.78, 20.2) * mm, v(15.3, 20.5) * mm, v(14.72, 20.18) * mm, v(14.19, 19.26) * mm, v(13.87, 18.12) * mm, v(14.01, 17.57) * mm, v(14.47, 17.36) * mm, v(14.88, 17.37) * mm, v(14.85, 16.99) * mm, v(14.54, 16.69) * mm, v(14.36, 16.48) * mm, v(14.35, 16.17) * mm, v(14.65, 15.92) * mm, v(15.07, 16.06) * mm, v(15.66, 16.5) * mm, v(16.25, 17.15) * mm, v(16.38, 17.77) * mm, v(16.3, 17.78) * mm, v(16.2, 17.77) * mm, v(16.15, 17.57) * mm, v(15.84, 17.02) * mm, v(15.15, 16.41) * mm, v(14.8, 16.25) * mm, v(14.7, 16.4) * mm, v(15.02, 16.7) * mm, v(15.15, 17.3) * mm, v(15.07, 17.6) * mm, v(14.63, 17.6) * mm, v(14.28, 17.75) * mm, v(14.34, 18.68) * mm, v(14.68, 19.6) * mm, v(15.01, 20.1) * mm, v(15.28, 20.14) * mm, v(15.62, 19.88) * mm, v(15.92, 19.32) * mm, v(15.97, 18.83) * mm, v(16.1, 18.63) * mm]});
            skFitSpline(sketch, "E98", {"points": [v(-2.9, 7.5) * mm, v(-3.28, 6.92) * mm, v(-4.38, 5.93) * mm, v(-5.16, 4.67) * mm, v(-5.23, 4.13) * mm, v(-4.95, 4.15) * mm, v(-4.8, 4.76) * mm, v(-4.1, 5.8) * mm, v(-3.25, 6.45) * mm, v(-2.7, 7.18) * mm, v(-2.7, 7.41) * mm, v(-2.9, 7.5) * mm]});
            skFitSpline(sketch, "E99", {"points": [v(-4.93, 3.87) * mm, v(-4.6, 3.55) * mm, v(-4.23, 3.2) * mm, v(-4, 2.46) * mm, v(-3.88, 1.57) * mm, v(-3.9, 1.05) * mm, v(-3.8, 1.02) * mm, v(-3.65, 1.1) * mm, v(-3.62, 1.54) * mm, v(-3.7, 2.58) * mm, v(-3.93, 3.3) * mm, v(-4.66, 4.04) * mm, v(-4.79, 4.14) * mm, v(-4.93, 3.87) * mm]});
            skFitSpline(sketch, "E100", {"points": [v(-5.5, 3.97) * mm, v(-5.38, 3.97) * mm, v(-5.28, 3.87) * mm, v(-5.59, 3.38) * mm, v(-6.36, 2.4) * mm, v(-6.5, 2.12) * mm, v(-6.43, 1.39) * mm, v(-6.33, 0.73) * mm, v(-6.65, 0) * mm, v(-7.41, -1.01) * mm, v(-8.12, -1.7) * mm, v(-8.3, -1.71) * mm, v(-8.32, -1.52) * mm, v(-7.93, -1.14) * mm, v(-7.13, -0.16) * mm, v(-6.7, 0.6) * mm, v(-6.72, 1.39) * mm, v(-6.8, 2.16) * mm, v(-5.99, 3.35) * mm, v(-5.5, 3.97) * mm]});
            skFitSpline(sketch, "E101", {"points": [v(-0.8, 7.39) * mm, v(-1.36, 7.33) * mm, v(-1.96, 7.01) * mm, v(-1.87, 6.81) * mm, v(-1.52, 6.94) * mm, v(-1.14, 7.1) * mm], "startDerivative": vector(-2.25, -0.05) * mm, "endDerivative": vector(1.9, 0.65) * mm});
            skFitSpline(sketch, "E102", {"points": [v(-1.14, 7.1) * mm, v(-1.14, 6.61) * mm, v(-1.36, 6.12) * mm, v(-2.14, 5.77) * mm, v(-2.84, 5.33) * mm, v(-3.28, 4.86) * mm, v(-3.23, 4.69) * mm, v(-3, 4.81) * mm, v(-2.74, 5.12) * mm, v(-2.19, 5.47) * mm, v(-1.46, 5.7) * mm, v(-1.02, 6.01) * mm, v(-0.78, 6.45) * mm, v(-0.85, 7.1) * mm, v(-0.6, 7.3) * mm, v(-0.52, 7.46) * mm, v(-0.7, 7.5) * mm, v(-0.8, 7.39) * mm], "startDerivative": vector(0.5, -7.75) * mm, "endDerivative": vector(-1.95, -4.35) * mm});
            skFitSpline(sketch, "E103", {"points": [v(1.92, 6.86) * mm, v(1.8, 6.35) * mm, v(1.25, 5.97) * mm, v(0.17, 5.45) * mm, v(-0.92, 4.48) * mm, v(-1.54, 3.63) * mm, v(-1.38, 3.42) * mm, v(-1.14, 3.75) * mm, v(0, 4.9) * mm, v(0.92, 5.38) * mm, v(1.66, 5.89) * mm], "startDerivative": vector(-0.48, -7.12) * mm, "endDerivative": vector(7.06, 5.37) * mm});
            skFitSpline(sketch, "E104", {"points": [v(1.66, 5.89) * mm, v(1.42, 5.29) * mm, v(1.06, 4.35) * mm, v(0.78, 3.57) * mm, v(0.87, 2.77) * mm, v(1.06, 2.7) * mm, v(1.04, 2.9) * mm, v(1, 3.38) * mm, v(1.42, 4.46) * mm, v(1.96, 5.89) * mm, v(2.17, 6.39) * mm, v(2.24, 6.94) * mm, v(1.92, 6.86) * mm], "startDerivative": vector(-2.75, -6.6) * mm, "endDerivative": vector(-6.73, -3.43) * mm});
            skFitSpline(sketch, "E105", {"points": [v(3.63, 6.66) * mm, v(3.31, 6.45) * mm, v(2.82, 6.16) * mm, v(2.28, 5.47) * mm, v(2.24, 5.27) * mm, v(2.46, 5.35) * mm, v(2.7, 5.7) * mm, v(3.26, 6.13) * mm, v(3.5, 5.96) * mm, v(3.67, 5.58) * mm, v(3.77, 5.5) * mm, v(3.81, 5.7) * mm, v(3.65, 6.16) * mm, v(3.59, 6.33) * mm, v(3.93, 6.65) * mm, v(3.63, 6.66) * mm]});
            skFitSpline(sketch, "E106", {"points": [v(10.74, 2.28) * mm, v(10.32, 1.61) * mm, v(10.12, 0.62) * mm, v(10.42, -0.78) * mm, v(10.52, -2.93) * mm, v(9.75, -4.73) * mm, v(8.72, -5.42) * mm, v(7.85, -5.7) * mm, v(7.52, -6.09) * mm, v(7.67, -6.24) * mm, v(7.92, -6) * mm, v(8.47, -5.8) * mm, v(9.1, -5.61) * mm, v(9.74, -5.14) * mm], "startDerivative": vector(-6.29, -8.62) * mm, "endDerivative": vector(8.65, 7.43) * mm});
            skFitSpline(sketch, "E107", {"points": [v(9.74, -5.14) * mm, v(9.36, -5.77) * mm, v(9.18, -6.3) * mm, v(9.26, -6.5) * mm, v(9.45, -6.41) * mm, v(9.57, -5.96) * mm, v(10.1, -5.14) * mm, v(10.7, -4.23) * mm, v(11.01, -3.02) * mm, v(10.83, -1.1) * mm, v(10.47, 0.45) * mm, v(10.62, 1.43) * mm, v(11.02, 2.07) * mm, v(10.74, 2.28) * mm], "startDerivative": vector(-5.35, -8.4) * mm, "endDerivative": vector(-7.95, 3.27) * mm});
            skFitSpline(sketch, "E108", {"points": [v(14.14, -1.36) * mm, v(13.97, -1.13) * mm, v(13.8, -1.15) * mm, v(13.78, -1.59) * mm, v(13.6, -2.97) * mm, v(13.55, -4.14) * mm, v(13.08, -4.55) * mm, v(12.29, -5.14) * mm, v(11.6, -6.13) * mm, v(11.53, -6.41) * mm, v(11.09, -6.86) * mm, v(10.74, -7.38) * mm, v(9.88, -7.38) * mm, v(8.67, -7.08) * mm, v(7.28, -6.66) * mm, v(6.03, -6.5) * mm, v(5.4, -6.86) * mm, v(4.65, -7.2) * mm, v(3.78, -7.32) * mm, v(2.57, -7.48) * mm, v(2, -7.73) * mm, v(2.08, -7.87) * mm, v(2.49, -7.78) * mm, v(3.4, -7.64) * mm, v(4.16, -7.68) * mm, v(5.27, -7.34) * mm, v(5.99, -6.93) * mm, v(6.68, -6.94) * mm, v(7.72, -7.14) * mm, v(8.7, -7.35) * mm, v(9.4, -7.62) * mm, v(10.52, -7.78) * mm], "startDerivative": vector(-7.62, 15.1) * mm, "endDerivative": vector(31.14, -2.42) * mm});
            skFitSpline(sketch, "E109", {"points": [v(14.14, -1.36) * mm, v(14.14, -1.76) * mm, v(14.14, -2) * mm, v(14.37, -1.77) * mm, v(14.52, -1.94) * mm, v(14.2, -2.25) * mm, v(13.96, -2.61) * mm, v(13.88, -3.37) * mm, v(13.84, -4.13) * mm, v(13.44, -4.73) * mm, v(12.94, -5.14) * mm, v(12.3, -5.76) * mm, v(11.9, -6.46) * mm, v(11.5, -6.85) * mm, v(11.26, -7.21) * mm], "startDerivative": vector(0.28, -5.98) * mm, "endDerivative": vector(-3.2, -5.83) * mm});
            skFitSpline(sketch, "E110", {"points": [v(11.26, -7.21) * mm, v(11.6, -6.98) * mm, v(12.4, -6.74) * mm, v(13.02, -6.6) * mm, v(13.07, -6.8) * mm, v(12.88, -6.92) * mm, v(11.98, -7.21) * mm, v(11.26, -7.69) * mm, v(10.82, -8.12) * mm, v(10.74, -9) * mm, v(10.52, -9.9) * mm, v(9.74, -11.08) * mm, v(9.35, -11.89) * mm, v(9.31, -13.28) * mm, v(9.03, -13.2) * mm, v(8.93, -12.45) * mm, v(9.1, -11.5) * mm, v(9.67, -10.6) * mm, v(10.2, -9.71) * mm, v(10.28, -9.36) * mm, v(10.28, -8.32) * mm, v(10.47, -7.92) * mm, v(10.52, -7.78) * mm], "startDerivative": vector(8.23, 7.31) * mm, "endDerivative": vector(2.05, 6.21) * mm});
            skFitSpline(sketch, "E111", {"points": [v(15.2, -3.16) * mm, v(14.94, -3.76) * mm, v(14.8, -4.52) * mm, v(14.74, -5.14) * mm, v(14.7, -5.76) * mm, v(14.32, -6.14) * mm, v(13.44, -6.46) * mm, v(13.44, -6.6) * mm, v(13.8, -6.6) * mm, v(14.48, -6.36) * mm, v(14.86, -5.95) * mm, v(14.97, -5.37) * mm, v(14.99, -4.73) * mm, v(15.13, -3.97) * mm, v(15.33, -3.3) * mm, v(15.2, -3.16) * mm]});
            skFitSpline(sketch, "E112", {"points": [v(12.53, -8.5) * mm, v(12.21, -9.42) * mm, v(12.27, -10.14) * mm, v(12.7, -10.6) * mm, v(13.58, -10.67) * mm, v(14.66, -10.96) * mm, v(15.16, -11.21) * mm, v(15.34, -11.4) * mm], "startDerivative": vector(-2.4, -5.6) * mm, "endDerivative": vector(1.76, -2.3) * mm});
            skFitSpline(sketch, "E113", {"points": [v(15.34, -11.4) * mm, v(14.9, -11.5) * mm, v(14.52, -11.89) * mm, v(14.45, -12.63) * mm, v(14.32, -14.2) * mm, v(13.58, -15.2) * mm, v(12.14, -15.8) * mm, v(9.86, -16.78) * mm, v(8.48, -18.29) * mm, v(8.7, -18.45) * mm, v(9.4, -17.73) * mm, v(10.42, -16.94) * mm, v(12.07, -16.24) * mm, v(13.58, -15.74) * mm, v(14.37, -14.82) * mm, v(14.76, -13.75) * mm, v(14.79, -12.54) * mm, v(15.03, -11.86) * mm, v(15.44, -11.67) * mm, v(15.56, -11.56) * mm, v(15.78, -11.81) * mm, v(16.26, -11.77) * mm, v(16.68, -11.8) * mm, v(16.92, -12.01) * mm, v(17.16, -12.02) * mm, v(17.38, -12.2) * mm, v(17.85, -11.73) * mm], "startDerivative": vector(-15.98, -1.47) * mm, "endDerivative": vector(14.89, 21.24) * mm});
            skFitSpline(sketch, "E114", {"points": [v(17.85, -11.73) * mm, v(17.67, -11.73) * mm, v(17.42, -11.93) * mm, v(17.13, -11.73) * mm, v(16.75, -11.4) * mm, v(16.09, -11.4) * mm, v(15.84, -11.3) * mm, v(15.27, -10.8) * mm, v(13.91, -10.46) * mm, v(13, -10.4) * mm, v(12.6, -9.84) * mm, v(12.82, -8.8) * mm, v(12.53, -8.5) * mm], "startDerivative": vector(-3.83, 1.06) * mm, "endDerivative": vector(-5.6, 3.05) * mm});
            skFitSpline(sketch, "E115", {"points": [v(11.6, -21.42) * mm, v(11.17, -21.22) * mm, v(10.24, -21.32) * mm, v(9.5, -21.32) * mm, v(9.23, -21.44) * mm, v(8.82, -21.46) * mm, v(8.44, -21.73) * mm, v(7.97, -21.91) * mm, v(7.3, -21.62) * mm, v(6.47, -20.96) * mm, v(5.74, -20.98) * mm, v(4.1, -21.44) * mm, v(3, -21.6) * mm, v(2.34, -21.24) * mm, v(2.16, -21.2) * mm, v(2, -20.4) * mm, v(1.79, -19.56) * mm, v(1.53, -19.7) * mm, v(1.63, -20.33) * mm, v(1.63, -21) * mm, v(1.9, -21.46) * mm], "startDerivative": vector(-9.02, 6.27) * mm, "endDerivative": vector(8.07, -9.37) * mm});
            skFitSpline(sketch, "E116", {"points": [v(1.9, -21.46) * mm, v(1.16, -21.66) * mm, v(0.12, -22.2) * mm, v(0.22, -22.29) * mm, v(0.53, -22.15) * mm, v(1.28, -21.84) * mm, v(2.23, -21.74) * mm, v(2.7, -22.05) * mm, v(5.01, -21.6) * mm, v(6.08, -21.46) * mm, v(6.45, -21.58) * mm, v(7.05, -22.12) * mm, v(7.75, -22.44) * mm, v(8.46, -22.2) * mm, v(8.79, -22.07) * mm, v(8.93, -21.88) * mm, v(9.55, -21.86) * mm, v(9.83, -21.69) * mm, v(10.18, -21.69) * mm, v(10.94, -21.6) * mm, v(11.57, -21.58) * mm, v(11.6, -21.42) * mm], "startDerivative": vector(-11.66, -2.52) * mm, "endDerivative": vector(-0.43, 7.74) * mm});
            skFitSpline(sketch, "E117", {"points": [v(4.48, -24.74) * mm, v(5.07, -24.62) * mm, v(5.49, -24.78) * mm, v(6.12, -24.88) * mm, v(6.52, -25.01) * mm, v(6.65, -24.88) * mm, v(6.73, -24.58) * mm, v(7.05, -24.3) * mm, v(7.25, -23.9) * mm, v(7.48, -23.98) * mm, v(7.4, -24.38) * mm, v(7.08, -24.8) * mm, v(6.86, -25.34) * mm, v(7.18, -25.95) * mm, v(7.64, -26.33) * mm, v(8.47, -27.23) * mm, v(8.97, -27.9) * mm, v(9.08, -28.7) * mm, v(9.17, -29.15) * mm, v(9.58, -28.93) * mm, v(10.28, -28.62) * mm, v(10.81, -28.6) * mm, v(10.66, -28.97) * mm, v(10.28, -29.11) * mm, v(9.95, -29.22) * mm, v(9.43, -29.5) * mm, v(9.14, -29.56) * mm, v(9.04, -29.94) * mm, v(8.8, -30.53) * mm, v(8.44, -30.72) * mm, v(8.56, -30.28) * mm, v(8.83, -29.61) * mm, v(8.77, -28.6) * mm, v(8.11, -27.47) * mm, v(7.4, -26.7) * mm, v(6.72, -26.1) * mm, v(6.28, -25.47) * mm, v(6.35, -25.27) * mm, v(5.99, -25.15) * mm, v(5.67, -25.14) * mm, v(5.3, -24.98) * mm, v(4.64, -24.9) * mm, v(4.48, -24.74) * mm]});
            skFitSpline(sketch, "E118", {"points": [v(1.84, -24.15) * mm, v(1.72, -24.4) * mm, v(1.92, -24.9) * mm, v(2.26, -25.51) * mm, v(2.75, -26.19) * mm, v(2.95, -26.6) * mm, v(3.57, -27.11) * mm, v(4.17, -27.47) * mm, v(5.2, -28.22) * mm, v(5.72, -28.96) * mm, v(6.38, -29.55) * mm, v(6.46, -30.44) * mm, v(6.37, -31.55) * mm, v(6.34, -31.9) * mm, v(6.67, -31.78) * mm, v(6.74, -31.55) * mm, v(6.78, -31) * mm, v(6.77, -30.32) * mm, v(6.97, -30.27) * mm, v(7.49, -30.45) * mm, v(7.83, -30.58) * mm, v(8.02, -30.43) * mm, v(7.71, -30.26) * mm, v(7.1, -30) * mm, v(6.78, -29.88) * mm, v(6.76, -29.57) * mm, v(6.52, -29.26) * mm, v(6.04, -28.83) * mm, v(5.67, -28.3) * mm, v(5.1, -27.68) * mm, v(4.47, -27.39) * mm, v(3.66, -26.8) * mm, v(3.17, -26.35) * mm, v(2.67, -25.49) * mm, v(2.23, -24.98) * mm, v(2.03, -24.43) * mm, v(2, -24.18) * mm, v(1.84, -24.15) * mm]});
            skFitSpline(sketch, "E119", {"points": [v(1.51, -25.14) * mm, v(1.36, -24.98) * mm, v(0.62, -24.98) * mm, v(0, -25.49) * mm, v(0.27, -25.49) * mm, v(0.54, -25.34) * mm, v(1.09, -25.29) * mm, v(1.37, -25.3) * mm, v(1.51, -25.14) * mm]});
            skFitSpline(sketch, "E120", {"points": [v(4.96, -28.92) * mm, v(5.09, -28.89) * mm, v(5.18, -29) * mm, v(5.3, -29.37) * mm, v(5.3, -30.58) * mm, v(5.3, -31.3) * mm, v(5.03, -31.8) * mm, v(4.64, -32.16) * mm, v(4.1, -32.6) * mm, v(3.86, -32.99) * mm, v(3.68, -32.87) * mm, v(3.93, -32.42) * mm, v(4.43, -31.87) * mm, v(4.9, -31.4) * mm, v(4.9, -30.51) * mm, v(4.87, -29.31) * mm, v(4.96, -28.92) * mm]});
            skFitSpline(sketch, "E121", {"points": [v(4.45, -28.01) * mm, v(4.64, -28.02) * mm, v(4.87, -28.23) * mm, v(4.92, -28.63) * mm, v(4.84, -28.77) * mm, v(4.71, -28.55) * mm, v(4.5, -28.25) * mm, v(4.4, -28.08) * mm, v(4.45, -28.01) * mm]});
            skFitSpline(sketch, "E122", {"points": [v(-4.81, -27.33) * mm, v(-4.91, -28.1) * mm, v(-4.81, -29.7) * mm, v(-4.52, -30.86) * mm, v(-3.5, -31.91) * mm, v(-3.16, -32.68) * mm, v(-3.83, -33.17) * mm, v(-4.74, -33.74) * mm, v(-4.57, -33.94) * mm, v(-4.1, -33.91) * mm, v(-3.95, -33.69) * mm, v(-3.26, -33.34) * mm, v(-2.92, -32.93) * mm, v(-2.52, -33.2) * mm, v(-2.18, -33.61) * mm, v(-2.15, -33.86) * mm, v(-1.8, -33.89) * mm, v(-1.86, -33.52) * mm, v(-2.18, -33) * mm, v(-2.74, -32.6) * mm], "startDerivative": vector(-2.35, -11.87) * mm, "endDerivative": vector(-11.52, 6.6) * mm});
            skFitSpline(sketch, "E123", {"points": [v(-2.74, -32.6) * mm, v(-2.92, -31.99) * mm, v(-3.6, -31.22) * mm, v(-4.14, -30.41) * mm, v(-4.4, -29.15) * mm, v(-4.51, -27.66) * mm, v(-4.81, -27.33) * mm], "startDerivative": vector(-0.59, 4.5) * mm, "endDerivative": vector(-3.08, 2.02) * mm});
            skFitSpline(sketch, "E124", {"points": [v(-14.5, 30.95) * mm, v(-15.53, 29.49) * mm, v(-16.8, 25.7) * mm, v(-17.4, 22.38) * mm, v(-16.8, 24.24) * mm, v(-15.9, 27.4) * mm, v(-14.5, 30.95) * mm]});
            skFitSpline(sketch, "E125", {"points": [v(-15.83, 25.23) * mm, v(-15.93, 23.94) * mm, v(-15.97, 21.08) * mm, v(-15.23, 17) * mm, v(-15.53, 20.02) * mm, v(-15.7, 22.74) * mm, v(-15.83, 25.23) * mm]});
            skFitSpline(sketch, "E126", {"points": [v(-10.62, 25.96) * mm, v(-11.31, 24.37) * mm, v(-11.51, 21.51) * mm, v(-11.18, 17.96) * mm, v(-11.15, 20.32) * mm, v(-11.11, 22.84) * mm, v(-10.88, 24.67) * mm, v(-10.62, 25.96) * mm]});
            skFitSpline(sketch, "E127", {"points": [v(9.6, 43.36) * mm, v(9.45, 42.24) * mm, v(8.75, 41.23) * mm, v(7.83, 40.32) * mm, v(7.6, 39.47) * mm, v(8.36, 38.96) * mm, v(10.41, 37.85) * mm, v(11.28, 37.4) * mm], "startDerivative": vector(-0.33, -8.35) * mm, "endDerivative": vector(5.81, -2.93) * mm});
            skFitSpline(sketch, "E128", {"points": [v(9.6, 43.36) * mm, v(9.82, 42.87) * mm, v(8.95, 40.97) * mm, v(8.3, 40.3) * mm, v(8.02, 39.83) * mm, v(8.2, 39.4) * mm, v(9.15, 38.98) * mm, v(9.96, 38.52) * mm, v(11.28, 37.4) * mm], "startDerivative": vector(3.6, -4.06) * mm, "endDerivative": vector(8.46, -7.56) * mm});
            skFitSpline(sketch, "E129", {"points": [v(12.94, 40.07) * mm, v(14.1, 39.75) * mm, v(16.06, 38.49) * mm, v(17.52, 36.63) * mm, v(18.15, 35.27) * mm], "startDerivative": vector(5.38, -1.02) * mm, "endDerivative": vector(2.35, -5.8) * mm});
            skFitSpline(sketch, "E130", {"points": [v(12.94, 40.07) * mm, v(14.64, 39.18) * mm, v(16.14, 37.85) * mm, v(18.15, 35.27) * mm], "startDerivative": vector(5.87, -2.74) * mm, "endDerivative": vector(5.26, -7.16) * mm});
            skFitSpline(sketch, "E131", {"points": [v(-8.55, -10.6) * mm, v(-8.4, -10.32) * mm, v(-7.62, -9.94) * mm, v(-6.24, -9.55) * mm, v(-4.88, -9.45) * mm], "startDerivative": vector(0.63, 2) * mm, "endDerivative": vector(4.47, 0.1) * mm});
            skFitSpline(sketch, "E132", {"points": [v(-8.55, -10.6) * mm, v(-8.34, -10.7) * mm, v(-7.88, -10.5) * mm, v(-6.6, -9.96) * mm, v(-4.88, -9.45) * mm], "startDerivative": vector(1.5, -1.2) * mm, "endDerivative": vector(4.86, 1.29) * mm});
            skFitSpline(sketch, "E133", {"points": [v(-7.78, -11.07) * mm, v(-7.5, -10.99) * mm, v(-6.62, -11.04) * mm, v(-6.61, -11.18) * mm, v(-6.9, -11.15) * mm, v(-7.59, -11.18) * mm, v(-7.81, -11.22) * mm, v(-7.78, -11.07) * mm]});
            skFitSpline(sketch, "E134", {"points": [v(-7.27, -11.36) * mm, v(-6.48, -11.26) * mm, v(-5.5, -11.29) * mm, v(-4.55, -11.52) * mm, v(-4.56, -11.68) * mm, v(-4.78, -11.6) * mm, v(-5.52, -11.46) * mm, v(-6.61, -11.45) * mm, v(-7.27, -11.49) * mm, v(-7.34, -11.41) * mm, v(-7.27, -11.36) * mm]});
            skFitSpline(sketch, "E135", {"points": [v(-7.23, -12.12) * mm, v(-7.01, -12.02) * mm, v(-6.32, -11.99) * mm, v(-5.56, -12.2) * mm, v(-5.17, -12.44) * mm, v(-5.18, -12.6) * mm, v(-5.41, -12.48) * mm, v(-6, -12.26) * mm, v(-6.72, -12.19) * mm, v(-7.15, -12.27) * mm, v(-7.23, -12.2) * mm, v(-7.23, -12.12) * mm]});
            skFitSpline(sketch, "E136", {"points": [v(-7.04, -12.38) * mm, v(-6.71, -12.33) * mm, v(-5.9, -12.45) * mm, v(-5.2, -12.85) * mm, v(-5.17, -13.01) * mm, v(-5.28, -13.04) * mm, v(-5.46, -12.84) * mm, v(-5.97, -12.6) * mm, v(-6.67, -12.52) * mm, v(-7.06, -12.5) * mm, v(-7.04, -12.38) * mm]});
            skFitSpline(sketch, "E137", {"points": [v(-7.22, -12.96) * mm, v(-7.1, -12.88) * mm, v(-6.89, -12.94) * mm, v(-6.54, -13.13) * mm, v(-6.35, -13.35) * mm, v(-6.42, -13.42) * mm, v(-6.5, -13.35) * mm, v(-6.73, -13.2) * mm, v(-7.06, -13.07) * mm, v(-7.22, -12.96) * mm]});
            skFitSpline(sketch, "E138", {"points": [v(-7.42, -13.26) * mm, v(-7.27, -13.26) * mm, v(-7.03, -13.43) * mm, v(-6.52, -13.69) * mm, v(-5.99, -14.02) * mm, v(-5.4, -14.47) * mm, v(-4.8, -15.14) * mm, v(-4.44, -15.74) * mm, v(-4.18, -16.15) * mm, v(-4.2, -16.41) * mm], "startDerivative": vector(2.45, 0.44) * mm, "endDerivative": vector(-0.94, -3.19) * mm});
            skFitSpline(sketch, "E139", {"points": [v(-7.42, -13.26) * mm, v(-7.42, -13.39) * mm, v(-7.13, -13.58) * mm, v(-6.56, -13.86) * mm, v(-5.93, -14.28) * mm, v(-5.45, -14.72) * mm, v(-4.94, -15.27) * mm, v(-4.47, -16.09) * mm, v(-4.32, -16.33) * mm, v(-4.2, -16.41) * mm], "startDerivative": vector(-0.55, -2.19) * mm, "endDerivative": vector(2.06, -1.13) * mm});
            skFitSpline(sketch, "E140", {"points": [v(-7.67, -14.51) * mm, v(-7.71, -14.63) * mm, v(-7.51, -14.84) * mm, v(-6.9, -15.57) * mm, v(-6.35, -16.41) * mm, v(-6.03, -17.2) * mm, v(-5.94, -17.76) * mm, v(-5.76, -17.82) * mm, v(-5.71, -17.56) * mm, v(-5.88, -16.78) * mm, v(-6.36, -15.92) * mm, v(-7, -15.08) * mm, v(-7.54, -14.54) * mm, v(-7.67, -14.51) * mm]});
            skFitSpline(sketch, "E141", {"points": [v(-7.6, -15.57) * mm, v(-7.63, -15.77) * mm, v(-7.2, -16.38) * mm, v(-6.78, -17.1) * mm, v(-6.7, -17.54) * mm, v(-6.52, -17.57) * mm, v(-6.52, -17.31) * mm, v(-6.8, -16.56) * mm, v(-7.2, -15.92) * mm, v(-7.51, -15.58) * mm, v(-7.6, -15.57) * mm]});
            skFitSpline(sketch, "E142", {"points": [v(-8.35, -16.47) * mm, v(-8.3, -16.6) * mm, v(-8.07, -16.99) * mm, v(-7.6, -17.9) * mm, v(-7.5, -19.38) * mm, v(-7.6, -20.43) * mm, v(-7.43, -20.43) * mm, v(-7.3, -19.99) * mm, v(-7.17, -18.96) * mm, v(-7.3, -18.04) * mm, v(-7.65, -17.17) * mm, v(-8.12, -16.41) * mm, v(-8.28, -16.41) * mm, v(-8.35, -16.47) * mm]});
            skFitSpline(sketch, "E143", {"points": [v(-9.5, -17.13) * mm, v(-9.5, -17.31) * mm, v(-9.34, -17.69) * mm, v(-9.12, -18.54) * mm, v(-9.03, -19.44) * mm, v(-9.05, -20.24) * mm, v(-8.86, -20.14) * mm, v(-8.8, -19.9) * mm, v(-8.8, -19.05) * mm, v(-8.93, -18.45) * mm, v(-9.2, -17.44) * mm, v(-9.38, -17.09) * mm, v(-9.5, -17.13) * mm]});
            skFitSpline(sketch, "E144", {"points": [v(-9.97, -17.82) * mm, v(-10.04, -17.96) * mm, v(-9.93, -18.22) * mm, v(-9.85, -18.84) * mm, v(-9.88, -19.63) * mm, v(-10.01, -19.92) * mm, v(-9.94, -20.06) * mm, v(-9.73, -19.88) * mm, v(-9.6, -19.34) * mm, v(-9.67, -18.58) * mm, v(-9.72, -18) * mm, v(-9.83, -17.82) * mm, v(-9.97, -17.82) * mm]});
            skFitSpline(sketch, "E145", {"points": [v(-10.5, -18.18) * mm, v(-10.47, -18.81) * mm, v(-10.52, -19.64) * mm, v(-10.64, -20.31) * mm, v(-10.54, -20.4) * mm, v(-10.33, -20.08) * mm, v(-10.26, -19.44) * mm, v(-10.26, -18.5) * mm, v(-10.32, -18.17) * mm, v(-10.4, -18.15) * mm, v(-10.5, -18.18) * mm]});
            skFitSpline(sketch, "E146", {"points": [v(-10.82, -18.62) * mm, v(-10.84, -19.2) * mm, v(-11.02, -19.83) * mm, v(-11.02, -19.93) * mm, v(-10.93, -19.97) * mm, v(-10.75, -19.7) * mm, v(-10.63, -19) * mm, v(-10.65, -18.62) * mm, v(-10.74, -18.58) * mm, v(-10.82, -18.62) * mm]});
            skFitSpline(sketch, "E147", {"points": [v(-11.13, -19) * mm, v(-11.24, -19.39) * mm, v(-11.61, -20.3) * mm, v(-11.59, -20.36) * mm, v(-11.46, -20.35) * mm, v(-11.3, -20.08) * mm, v(-11.09, -19.57) * mm, v(-11.01, -19.06) * mm, v(-11.06, -19) * mm, v(-11.13, -19) * mm]});
            skFitSpline(sketch, "E148", {"points": [v(-13.27, -20.37) * mm, v(-12.92, -19.76) * mm, v(-12.4, -18.63) * mm, v(-12.31, -17.92) * mm, v(-12.22, -17.58) * mm, v(-12.09, -17.65) * mm, v(-12.05, -17.67) * mm, v(-12.11, -18.46) * mm, v(-12.4, -19.25) * mm, v(-12.83, -20.08) * mm, v(-13.13, -20.41) * mm, v(-13.27, -20.37) * mm]});
            skFitSpline(sketch, "E149", {"points": [v(-12.93, -17.8) * mm, v(-12.8, -17.84) * mm, v(-12.7, -17.96) * mm, v(-12.81, -18.23) * mm, v(-13.18, -19.02) * mm, v(-13.85, -19.85) * mm, v(-14.38, -20.22) * mm, v(-14.4, -20.08) * mm, v(-14.22, -19.93) * mm, v(-13.74, -19.42) * mm, v(-13.2, -18.54) * mm, v(-12.97, -17.96) * mm, v(-12.93, -17.8) * mm]});
            skFitSpline(sketch, "E150", {"points": [v(-13.83, -18.07) * mm, v(-14.23, -18.57) * mm, v(-14.49, -18.98) * mm, v(-14.45, -19.15) * mm, v(-14.3, -19.16) * mm, v(-14.12, -18.95) * mm, v(-13.77, -18.47) * mm, v(-13.71, -18.2) * mm, v(-13.83, -18.07) * mm]});
            skFitSpline(sketch, "E151", {"points": [v(-14.57, -18.14) * mm, v(-14.85, -18.4) * mm, v(-15, -18.55) * mm, v(-14.9, -18.63) * mm, v(-14.77, -18.51) * mm, v(-14.53, -18.25) * mm, v(-14.49, -18.15) * mm, v(-14.57, -18.14) * mm]});
            skFitSpline(sketch, "E152", {"points": [v(-16.28, -18.83) * mm, v(-16.18, -18.61) * mm, v(-15.58, -18.14) * mm, v(-14.83, -17.65) * mm, v(-14.26, -17.24) * mm, v(-14.15, -17.22) * mm, v(-14.1, -17.31) * mm, v(-14.22, -17.4) * mm, v(-15.02, -17.96) * mm, v(-15.83, -18.55) * mm, v(-16.13, -18.85) * mm, v(-16.22, -18.88) * mm, v(-16.28, -18.83) * mm]});
            skFitSpline(sketch, "E153", {"points": [v(-15.23, -16.65) * mm, v(-15.63, -16.89) * mm, v(-16.13, -17.32) * mm, v(-16.44, -17.44) * mm, v(-16.35, -17.25) * mm, v(-16.01, -16.95) * mm, v(-15.67, -16.64) * mm, v(-15.36, -16.52) * mm, v(-15.22, -16.54) * mm, v(-15.2, -16.6) * mm, v(-15.23, -16.65) * mm]});
            skFitSpline(sketch, "E154", {"points": [v(-17.04, -17.28) * mm, v(-16.66, -16.92) * mm, v(-16, -16.52) * mm, v(-15.25, -16.17) * mm, v(-14.86, -16.1) * mm, v(-14.8, -15.97) * mm, v(-14.97, -15.88) * mm, v(-15.14, -16) * mm, v(-15.63, -16.16) * mm, v(-16.23, -16.45) * mm, v(-16.96, -16.93) * mm, v(-17.2, -17.24) * mm, v(-17.15, -17.3) * mm, v(-17.04, -17.28) * mm]});
            skFitSpline(sketch, "E155", {"points": [v(-18.06, -15.6) * mm, v(-17.81, -15.35) * mm, v(-17.35, -15.08) * mm, v(-16.68, -14.87) * mm, v(-16.03, -14.82) * mm, v(-15.42, -14.7) * mm, v(-15.32, -14.78) * mm, v(-15.4, -14.88) * mm, v(-16.09, -15) * mm, v(-16.8, -15.09) * mm, v(-17.58, -15.47) * mm, v(-17.88, -15.77) * mm, v(-18, -15.8) * mm, v(-18.04, -15.7) * mm, v(-18.06, -15.6) * mm]});
            skFitSpline(sketch, "E156", {"points": [v(-18.33, -13.9) * mm, v(-18.1, -13.65) * mm, v(-17.58, -13.46) * mm, v(-16.93, -13.34) * mm, v(-16.03, -13.54) * mm, v(-15.84, -13.6) * mm, v(-15.88, -13.8) * mm, v(-16.06, -13.74) * mm, v(-16.68, -13.59) * mm, v(-17.41, -13.6) * mm, v(-17.96, -13.86) * mm, v(-18.27, -14.1) * mm, v(-18.33, -13.9) * mm]});
            skFitSpline(sketch, "E157", {"points": [v(-17.23, -12.84) * mm, v(-17.03, -12.77) * mm, v(-16.74, -12.77) * mm, v(-16.26, -12.9) * mm, v(-16.26, -13.02) * mm, v(-16.48, -12.97) * mm, v(-17.15, -12.96) * mm, v(-17.27, -12.9) * mm, v(-17.23, -12.84) * mm]});
            skFitSpline(sketch, "E158", {"points": [v(-16.86, -11.66) * mm, v(-16.64, -11.93) * mm, v(-16.24, -12.27) * mm, v(-15.97, -12.42) * mm, v(-15.87, -12.32) * mm, v(-15.94, -12.14) * mm, v(-16.24, -11.91) * mm, v(-16.62, -11.54) * mm, v(-16.78, -11.53) * mm, v(-16.86, -11.66) * mm]});
            skFitSpline(sketch, "E159", {"points": [v(-16.48, -9.33) * mm, v(-16.49, -9.64) * mm, v(-16.26, -10) * mm, v(-15.75, -10.72) * mm, v(-15.3, -11.3) * mm, v(-15.12, -11.7) * mm, v(-15.03, -11.79) * mm, v(-14.96, -11.65) * mm, v(-15, -11.25) * mm, v(-15.27, -11) * mm, v(-15.77, -10.34) * mm, v(-16.23, -9.55) * mm, v(-16.35, -9.28) * mm, v(-16.48, -9.33) * mm]});
            skFitSpline(sketch, "E160", {"points": [v(-15.74, -9.43) * mm, v(-15.78, -9.63) * mm, v(-15.7, -9.88) * mm, v(-15.44, -10.44) * mm, v(-14.98, -11.03) * mm, v(-14.96, -10.9) * mm, v(-15.07, -10.72) * mm, v(-15.36, -10.24) * mm, v(-15.55, -9.78) * mm, v(-15.6, -9.47) * mm, v(-15.74, -9.43) * mm]});
            skFitSpline(sketch, "E161", {"points": [v(-15.13, -10.02) * mm, v(-15, -10.33) * mm, v(-14.9, -10.78) * mm, v(-14.8, -10.81) * mm, v(-14.72, -10.7) * mm, v(-14.77, -10.4) * mm, v(-14.89, -10.09) * mm, v(-15.02, -9.96) * mm, v(-15.13, -10.02) * mm]});
            skFitSpline(sketch, "E162", {"points": [v(-14.48, -7.76) * mm, v(-14.68, -8.26) * mm, v(-14.75, -9.02) * mm, v(-14.48, -9.92) * mm, v(-14.22, -10.4) * mm, v(-14.03, -10.5) * mm, v(-13.91, -10.4) * mm, v(-14.06, -10.21) * mm, v(-14.35, -9.72) * mm, v(-14.5, -9.21) * mm, v(-14.48, -8.44) * mm, v(-14.26, -7.99) * mm, v(-14.23, -7.76) * mm, v(-14.34, -7.71) * mm, v(-14.48, -7.76) * mm]});
            skFitSpline(sketch, "E163", {"points": [v(-14.2, -8.22) * mm, v(-14.34, -8.5) * mm, v(-14.4, -9.03) * mm, v(-14.25, -9.67) * mm, v(-13.97, -10) * mm, v(-13.86, -9.92) * mm, v(-13.86, -9.78) * mm, v(-14.07, -9.55) * mm, v(-14.18, -8.88) * mm, v(-14.07, -8.25) * mm, v(-14.08, -8.19) * mm, v(-14.2, -8.22) * mm]});
            skFitSpline(sketch, "E164", {"points": [v(-13.76, -8.15) * mm, v(-13.96, -8.6) * mm, v(-13.96, -9.13) * mm, v(-13.75, -9.55) * mm, v(-13.54, -9.73) * mm, v(-13.49, -9.55) * mm, v(-13.5, -9.47) * mm, v(-13.63, -9.32) * mm, v(-13.74, -8.76) * mm, v(-13.6, -8.26) * mm, v(-13.65, -8.16) * mm, v(-13.76, -8.15) * mm]});
            skFitSpline(sketch, "E165", {"points": [v(-11.96, -6.8) * mm, v(-12.17, -7.21) * mm, v(-12.44, -7.96) * mm, v(-12.42, -9.06) * mm, v(-12.37, -9.47) * mm, v(-12.22, -9.47) * mm, v(-12.23, -9.31) * mm, v(-12.23, -8.9) * mm, v(-12.24, -8.28) * mm, v(-12, -7.42) * mm, v(-11.75, -7) * mm, v(-11.76, -6.81) * mm, v(-11.9, -6.76) * mm, v(-11.96, -6.8) * mm]});
            skFitSpline(sketch, "E166", {"points": [v(-11.57, -7.5) * mm, v(-11.76, -7.78) * mm, v(-11.97, -8.25) * mm, v(-11.97, -8.72) * mm, v(-11.91, -9.06) * mm, v(-11.76, -9.05) * mm, v(-11.77, -8.72) * mm, v(-11.73, -8.17) * mm, v(-11.53, -7.82) * mm, v(-11.46, -7.6) * mm, v(-11.57, -7.5) * mm]});
            skFitSpline(sketch, "E167", {"points": [v(-11.03, -7.45) * mm, v(-11.25, -7.67) * mm, v(-11.43, -7.97) * mm, v(-11.66, -8.52) * mm, v(-11.66, -8.8) * mm, v(-11.64, -8.95) * mm, v(-11.48, -8.93) * mm, v(-11.4, -8.66) * mm, v(-11.3, -8.24) * mm, v(-11, -7.75) * mm, v(-10.95, -7.53) * mm, v(-11.03, -7.45) * mm]});
            skFitSpline(sketch, "E168", {"points": [v(-10.03, -7.86) * mm, v(-10.4, -8.11) * mm, v(-10.81, -8.7) * mm, v(-10.94, -9.08) * mm, v(-10.94, -9.21) * mm, v(-10.85, -9.28) * mm, v(-10.66, -8.95) * mm, v(-10.45, -8.6) * mm, v(-10.07, -8.18) * mm, v(-9.92, -8) * mm, v(-9.96, -7.88) * mm, v(-10.03, -7.86) * mm]});
            skFitSpline(sketch, "E169", {"points": [v(-10.12, -8.93) * mm, v(-9.6, -8.3) * mm, v(-8.68, -7.61) * mm, v(-7.85, -7.17) * mm, v(-7.88, -7.34) * mm, v(-8.4, -7.67) * mm, v(-9.37, -8.46) * mm, v(-9.75, -8.82) * mm, v(-10.12, -8.93) * mm]});
            skFitSpline(sketch, "E170", {"points": [v(-7.78, -7.87) * mm, v(-8.55, -8.29) * mm, v(-9, -8.65) * mm, v(-9.37, -8.95) * mm, v(-9.54, -9.11) * mm, v(-9.47, -9.26) * mm, v(-9.14, -9.02) * mm, v(-8.62, -8.6) * mm, v(-8.12, -8.27) * mm, v(-7.7, -8.08) * mm, v(-7.68, -7.88) * mm, v(-7.78, -7.87) * mm]});
            skFitSpline(sketch, "E171", {"points": [v(-9.22, -9.73) * mm, v(-9.06, -9.4) * mm, v(-8.5, -8.95) * mm, v(-7.97, -8.7) * mm, v(-7.6, -8.52) * mm, v(-7.54, -8.65) * mm, v(-7.63, -8.76) * mm, v(-8, -8.95) * mm, v(-8.54, -9.25) * mm, v(-8.92, -9.6) * mm, v(-9.08, -9.78) * mm, v(-9.22, -9.73) * mm]});
            skFitSpline(sketch, "E172", {"points": [v(-8.54, -9.82) * mm, v(-8.36, -9.58) * mm, v(-7.98, -9.16) * mm, v(-7.85, -9.1) * mm, v(-7.69, -9.22) * mm, v(-7.87, -9.47) * mm, v(-8.27, -9.78) * mm, v(-8.45, -9.93) * mm, v(-8.54, -9.82) * mm]});
            skFitSpline(sketch, "E173", {"points": [v(17.2, 22.04) * mm, v(16.85, 21.72) * mm, v(16.47, 21.2) * mm, v(16.45, 20.82) * mm, v(16.6, 20.5) * mm, v(17.1, 20.75) * mm, v(17.4, 21.26) * mm, v(17.61, 21.73) * mm, v(17.5, 22.02) * mm, v(17.2, 22.04) * mm]});
            skSolve(sketch);
        }
        {
            var Q0;
            Q0=makeQuery(id+"F13.imprint","IMPRINT",FACE,{"disambiguationData":[TD([[makeQuery(id+"F13.imprint","IMPRINT",EDGE,{"derivedFrom":sQuery(id+"F13.wireOp",EDGE,"E89")}),1.0]])]});
            var Q1;
            Q1=makeQuery(id+"F13.imprint","IMPRINT",FACE,{"disambiguationData":[TD([[makeQuery(id+"F13.imprint","IMPRINT",EDGE,{"derivedFrom":sQuery(id+"F13.wireOp",EDGE,"E91")}),1.0]])]});
            var Q2;
            Q2=makeQuery(id+"F13.imprint","IMPRINT",FACE,{"disambiguationData":[TD([[makeQuery(id+"F13.imprint","IMPRINT",EDGE,{"derivedFrom":sQuery(id+"F13.wireOp",EDGE,"E95")}),1.0]])]});
            var Q3;
            Q3=makeQuery(id+"F13.imprint","IMPRINT",FACE,{"disambiguationData":[TD([[makeQuery(id+"F13.imprint","IMPRINT",EDGE,{"derivedFrom":sQuery(id+"F13.wireOp",EDGE,"E96")}),1.0]])]});
            var Q4;
            Q4=makeQuery(id+"F13.imprint","IMPRINT",FACE,{"disambiguationData":[TD([[makeQuery(id+"F13.imprint","IMPRINT",EDGE,{"derivedFrom":sQuery(id+"F13.wireOp",EDGE,"E93")}),1.0]])]});
            var Q5;
            Q5=makeQuery(id+"F13.imprint","IMPRINT",FACE,{"disambiguationData":[TD([[makeQuery(id+"F13.imprint","IMPRINT",EDGE,{"derivedFrom":sQuery(id+"F13.wireOp",EDGE,"E97")}),1.0]])]});
            extrude(context, id + "F14", {"entities" : qUnion([Q0, Q1, Q2, Q3, Q4, Q5]), "operationType" : NewBodyOperationType.ADD, "depth" : 4.75 * mm, "offsetDistance" : 25 * mm});
        }
        {
            var Q0;
            Q0=makeQuery(id+"F13.imprint","IMPRINT",FACE,{"disambiguationData":[TD([[makeQuery(id+"F13.imprint","IMPRINT",EDGE,{"derivedFrom":sQuery(id+"F13.wireOp",EDGE,"E98")}),1.0]])]});
            var Q1;
            Q1=makeQuery(id+"F13.imprint","IMPRINT",FACE,{"disambiguationData":[TD([[makeQuery(id+"F13.imprint","IMPRINT",EDGE,{"derivedFrom":sQuery(id+"F13.wireOp",EDGE,"E100")}),-1.0]])]});
            var Q2;
            Q2=makeQuery(id+"F13.imprint","IMPRINT",FACE,{"disambiguationData":[TD([[makeQuery(id+"F13.imprint","IMPRINT",EDGE,{"derivedFrom":sQuery(id+"F13.wireOp",EDGE,"E99")}),1.0]])]});
            var Q3;
            Q3=makeQuery(id+"F13.imprint","IMPRINT",FACE,{"disambiguationData":[TD([[makeQuery(id+"F13.imprint","IMPRINT",EDGE,{"derivedFrom":sQuery(id+"F13.wireOp",EDGE,"E101")}),1.0]])]});
            var Q4;
            Q4=makeQuery(id+"F13.imprint","IMPRINT",FACE,{"disambiguationData":[TD([[makeQuery(id+"F13.imprint","IMPRINT",EDGE,{"derivedFrom":sQuery(id+"F13.wireOp",EDGE,"E103")}),1.0]])]});
            var Q5;
            Q5=makeQuery(id+"F13.imprint","IMPRINT",FACE,{"disambiguationData":[TD([[makeQuery(id+"F13.imprint","IMPRINT",EDGE,{"derivedFrom":sQuery(id+"F13.wireOp",EDGE,"E105")}),1.0]])]});
            var Q6;
            Q6=makeQuery(id+"F13.imprint","IMPRINT",FACE,{"disambiguationData":[TD([[makeQuery(id+"F13.imprint","IMPRINT",EDGE,{"derivedFrom":sQuery(id+"F13.wireOp",EDGE,"E106")}),1.0]])]});
            var Q7;
            Q7=makeQuery(id+"F13.imprint","IMPRINT",FACE,{"disambiguationData":[TD([[makeQuery(id+"F13.imprint","IMPRINT",EDGE,{"derivedFrom":sQuery(id+"F13.wireOp",EDGE,"E108")}),1.0]])]});
            var Q8;
            Q8=makeQuery(id+"F13.imprint","IMPRINT",FACE,{"disambiguationData":[TD([[makeQuery(id+"F13.imprint","IMPRINT",EDGE,{"derivedFrom":sQuery(id+"F13.wireOp",EDGE,"E111")}),1.0]])]});
            var Q9;
            Q9=makeQuery(id+"F13.imprint","IMPRINT",FACE,{"disambiguationData":[TD([[makeQuery(id+"F13.imprint","IMPRINT",EDGE,{"derivedFrom":sQuery(id+"F13.wireOp",EDGE,"E112")}),1.0]])]});
            var Q10;
            Q10=makeQuery(id+"F13.imprint","IMPRINT",FACE,{"disambiguationData":[TD([[makeQuery(id+"F13.imprint","IMPRINT",EDGE,{"derivedFrom":sQuery(id+"F13.wireOp",EDGE,"E115")}),1.0]])]});
            var Q11;
            Q11=makeQuery(id+"F13.imprint","IMPRINT",FACE,{"disambiguationData":[TD([[makeQuery(id+"F13.imprint","IMPRINT",EDGE,{"derivedFrom":sQuery(id+"F13.wireOp",EDGE,"E117")}),-1.0]])]});
            var Q12;
            Q12=makeQuery(id+"F13.imprint","IMPRINT",FACE,{"disambiguationData":[TD([[makeQuery(id+"F13.imprint","IMPRINT",EDGE,{"derivedFrom":sQuery(id+"F13.wireOp",EDGE,"E118")}),1.0]])]});
            var Q13;
            Q13=makeQuery(id+"F13.imprint","IMPRINT",FACE,{"disambiguationData":[TD([[makeQuery(id+"F13.imprint","IMPRINT",EDGE,{"derivedFrom":sQuery(id+"F13.wireOp",EDGE,"E120")}),-1.0]])]});
            var Q14;
            Q14=makeQuery(id+"F13.imprint","IMPRINT",FACE,{"disambiguationData":[TD([[makeQuery(id+"F13.imprint","IMPRINT",EDGE,{"derivedFrom":sQuery(id+"F13.wireOp",EDGE,"E119")}),1.0]])]});
            var Q15;
            Q15=makeQuery(id+"F13.imprint","IMPRINT",FACE,{"disambiguationData":[TD([[makeQuery(id+"F13.imprint","IMPRINT",EDGE,{"derivedFrom":sQuery(id+"F13.wireOp",EDGE,"E121")}),-1.0]])]});
            var Q16;
            Q16=makeQuery(id+"F13.imprint","IMPRINT",FACE,{"disambiguationData":[TD([[makeQuery(id+"F13.imprint","IMPRINT",EDGE,{"derivedFrom":sQuery(id+"F13.wireOp",EDGE,"E122")}),1.0]])]});
            extrude(context, id + "F15", {"entities" : qUnion([Q0, Q1, Q2, Q3, Q4, Q5, Q6, Q7, Q8, Q9, Q10, Q11, Q12, Q13, Q14, Q15, Q16]), "operationType" : NewBodyOperationType.ADD, "depth" : 5.5 * mm, "offsetDistance" : 25 * mm});
        }
        {
            var Q0;
            Q0=makeQuery(id+"F13.imprint","IMPRINT",FACE,{"disambiguationData":[TD([[makeQuery(id+"F13.imprint","IMPRINT",EDGE,{"derivedFrom":sQuery(id+"F13.wireOp",EDGE,"E124")}),1.0]])]});
            var Q1;
            Q1=makeQuery(id+"F13.imprint","IMPRINT",FACE,{"disambiguationData":[TD([[makeQuery(id+"F13.imprint","IMPRINT",EDGE,{"derivedFrom":sQuery(id+"F13.wireOp",EDGE,"E125")}),1.0]])]});
            var Q2;
            Q2=makeQuery(id+"F13.imprint","IMPRINT",FACE,{"disambiguationData":[TD([[makeQuery(id+"F13.imprint","IMPRINT",EDGE,{"derivedFrom":sQuery(id+"F13.wireOp",EDGE,"E126")}),1.0]])]});
            var Q3;
            Q3=makeQuery(id+"F13.imprint","IMPRINT",FACE,{"disambiguationData":[TD([[makeQuery(id+"F13.imprint","IMPRINT",EDGE,{"derivedFrom":sQuery(id+"F13.wireOp",EDGE,"E127")}),1.0]])]});
            var Q4;
            Q4=makeQuery(id+"F13.imprint","IMPRINT",FACE,{"disambiguationData":[TD([[makeQuery(id+"F13.imprint","IMPRINT",EDGE,{"derivedFrom":sQuery(id+"F13.wireOp",EDGE,"E129")}),-1.0]])]});
            extrude(context, id + "F16", {"entities" : qUnion([Q0, Q1, Q2, Q3, Q4]), "operationType" : NewBodyOperationType.ADD, "depth" : 5.5 * mm, "offsetDistance" : 25 * mm});
        }
        {
            var Q0;
            Q0=makeQuery(id+"F13.imprint","IMPRINT",FACE,{"disambiguationData":[TD([[makeQuery(id+"F13.imprint","IMPRINT",EDGE,{"derivedFrom":sQuery(id+"F13.wireOp",EDGE,"E131")}),-1.0]])]});
            var Q1;
            Q1=makeQuery(id+"F13.imprint","IMPRINT",FACE,{"disambiguationData":[TD([[makeQuery(id+"F13.imprint","IMPRINT",EDGE,{"derivedFrom":sQuery(id+"F13.wireOp",EDGE,"E134")}),-1.0]])]});
            var Q2;
            Q2=makeQuery(id+"F13.imprint","IMPRINT",FACE,{"disambiguationData":[TD([[makeQuery(id+"F13.imprint","IMPRINT",EDGE,{"derivedFrom":sQuery(id+"F13.wireOp",EDGE,"E133")}),-1.0]])]});
            var Q3;
            Q3=makeQuery(id+"F13.imprint","IMPRINT",FACE,{"disambiguationData":[TD([[makeQuery(id+"F13.imprint","IMPRINT",EDGE,{"derivedFrom":sQuery(id+"F13.wireOp",EDGE,"E135")}),-1.0]])]});
            var Q4;
            Q4=makeQuery(id+"F13.imprint","IMPRINT",FACE,{"disambiguationData":[TD([[makeQuery(id+"F13.imprint","IMPRINT",EDGE,{"derivedFrom":sQuery(id+"F13.wireOp",EDGE,"E136")}),-1.0]])]});
            var Q5;
            Q5=makeQuery(id+"F13.imprint","IMPRINT",FACE,{"disambiguationData":[TD([[makeQuery(id+"F13.imprint","IMPRINT",EDGE,{"derivedFrom":sQuery(id+"F13.wireOp",EDGE,"E138")}),-1.0]])]});
            var Q6;
            Q6=makeQuery(id+"F13.imprint","IMPRINT",FACE,{"disambiguationData":[TD([[makeQuery(id+"F13.imprint","IMPRINT",EDGE,{"derivedFrom":sQuery(id+"F13.wireOp",EDGE,"E137")}),-1.0]])]});
            var Q7;
            Q7=makeQuery(id+"F13.imprint","IMPRINT",FACE,{"disambiguationData":[TD([[makeQuery(id+"F13.imprint","IMPRINT",EDGE,{"derivedFrom":sQuery(id+"F13.wireOp",EDGE,"E140")}),1.0]])]});
            var Q8;
            Q8=makeQuery(id+"F13.imprint","IMPRINT",FACE,{"disambiguationData":[TD([[makeQuery(id+"F13.imprint","IMPRINT",EDGE,{"derivedFrom":sQuery(id+"F13.wireOp",EDGE,"E141")}),1.0]])]});
            var Q9;
            Q9=makeQuery(id+"F13.imprint","IMPRINT",FACE,{"disambiguationData":[TD([[makeQuery(id+"F13.imprint","IMPRINT",EDGE,{"derivedFrom":sQuery(id+"F13.wireOp",EDGE,"E142")}),1.0]])]});
            var Q10;
            Q10=makeQuery(id+"F13.imprint","IMPRINT",FACE,{"disambiguationData":[TD([[makeQuery(id+"F13.imprint","IMPRINT",EDGE,{"derivedFrom":sQuery(id+"F13.wireOp",EDGE,"E143")}),1.0]])]});
            var Q11;
            Q11=makeQuery(id+"F13.imprint","IMPRINT",FACE,{"disambiguationData":[TD([[makeQuery(id+"F13.imprint","IMPRINT",EDGE,{"derivedFrom":sQuery(id+"F13.wireOp",EDGE,"E144")}),1.0]])]});
            var Q12;
            Q12=makeQuery(id+"F13.imprint","IMPRINT",FACE,{"disambiguationData":[TD([[makeQuery(id+"F13.imprint","IMPRINT",EDGE,{"derivedFrom":sQuery(id+"F13.wireOp",EDGE,"E145")}),1.0]])]});
            var Q13;
            Q13=makeQuery(id+"F13.imprint","IMPRINT",FACE,{"disambiguationData":[TD([[makeQuery(id+"F13.imprint","IMPRINT",EDGE,{"derivedFrom":sQuery(id+"F13.wireOp",EDGE,"E146")}),1.0]])]});
            var Q14;
            Q14=makeQuery(id+"F13.imprint","IMPRINT",FACE,{"disambiguationData":[TD([[makeQuery(id+"F13.imprint","IMPRINT",EDGE,{"derivedFrom":sQuery(id+"F13.wireOp",EDGE,"E147")}),1.0]])]});
            var Q15;
            Q15=makeQuery(id+"F13.imprint","IMPRINT",FACE,{"disambiguationData":[TD([[makeQuery(id+"F13.imprint","IMPRINT",EDGE,{"derivedFrom":sQuery(id+"F13.wireOp",EDGE,"E172")}),-1.0]])]});
            var Q16;
            Q16=makeQuery(id+"F13.imprint","IMPRINT",FACE,{"disambiguationData":[TD([[makeQuery(id+"F13.imprint","IMPRINT",EDGE,{"derivedFrom":sQuery(id+"F13.wireOp",EDGE,"E171")}),-1.0]])]});
            var Q17;
            Q17=makeQuery(id+"F13.imprint","IMPRINT",FACE,{"disambiguationData":[TD([[makeQuery(id+"F13.imprint","IMPRINT",EDGE,{"derivedFrom":sQuery(id+"F13.wireOp",EDGE,"E170")}),1.0]])]});
            var Q18;
            Q18=makeQuery(id+"F13.imprint","IMPRINT",FACE,{"disambiguationData":[TD([[makeQuery(id+"F13.imprint","IMPRINT",EDGE,{"derivedFrom":sQuery(id+"F13.wireOp",EDGE,"E169")}),-1.0]])]});
            var Q19;
            Q19=makeQuery(id+"F13.imprint","IMPRINT",FACE,{"disambiguationData":[TD([[makeQuery(id+"F13.imprint","IMPRINT",EDGE,{"derivedFrom":sQuery(id+"F13.wireOp",EDGE,"E168")}),1.0]])]});
            var Q20;
            Q20=makeQuery(id+"F13.imprint","IMPRINT",FACE,{"disambiguationData":[TD([[makeQuery(id+"F13.imprint","IMPRINT",EDGE,{"derivedFrom":sQuery(id+"F13.wireOp",EDGE,"E167")}),1.0]])]});
            var Q21;
            Q21=makeQuery(id+"F13.imprint","IMPRINT",FACE,{"disambiguationData":[TD([[makeQuery(id+"F13.imprint","IMPRINT",EDGE,{"derivedFrom":sQuery(id+"F13.wireOp",EDGE,"E166")}),1.0]])]});
            var Q22;
            Q22=makeQuery(id+"F13.imprint","IMPRINT",FACE,{"disambiguationData":[TD([[makeQuery(id+"F13.imprint","IMPRINT",EDGE,{"derivedFrom":sQuery(id+"F13.wireOp",EDGE,"E165")}),1.0]])]});
            var Q23;
            Q23=makeQuery(id+"F13.imprint","IMPRINT",FACE,{"disambiguationData":[TD([[makeQuery(id+"F13.imprint","IMPRINT",EDGE,{"derivedFrom":sQuery(id+"F13.wireOp",EDGE,"E164")}),1.0]])]});
            var Q24;
            Q24=makeQuery(id+"F13.imprint","IMPRINT",FACE,{"disambiguationData":[TD([[makeQuery(id+"F13.imprint","IMPRINT",EDGE,{"derivedFrom":sQuery(id+"F13.wireOp",EDGE,"E163")}),1.0]])]});
            var Q25;
            Q25=makeQuery(id+"F13.imprint","IMPRINT",FACE,{"disambiguationData":[TD([[makeQuery(id+"F13.imprint","IMPRINT",EDGE,{"derivedFrom":sQuery(id+"F13.wireOp",EDGE,"E162")}),1.0]])]});
            var Q26;
            Q26=makeQuery(id+"F13.imprint","IMPRINT",FACE,{"disambiguationData":[TD([[makeQuery(id+"F13.imprint","IMPRINT",EDGE,{"derivedFrom":sQuery(id+"F13.wireOp",EDGE,"E161")}),1.0]])]});
            var Q27;
            Q27=makeQuery(id+"F13.imprint","IMPRINT",FACE,{"disambiguationData":[TD([[makeQuery(id+"F13.imprint","IMPRINT",EDGE,{"derivedFrom":sQuery(id+"F13.wireOp",EDGE,"E160")}),1.0]])]});
            var Q28;
            Q28=makeQuery(id+"F13.imprint","IMPRINT",FACE,{"disambiguationData":[TD([[makeQuery(id+"F13.imprint","IMPRINT",EDGE,{"derivedFrom":sQuery(id+"F13.wireOp",EDGE,"E159")}),1.0]])]});
            var Q29;
            Q29=makeQuery(id+"F13.imprint","IMPRINT",FACE,{"disambiguationData":[TD([[makeQuery(id+"F13.imprint","IMPRINT",EDGE,{"derivedFrom":sQuery(id+"F13.wireOp",EDGE,"E158")}),1.0]])]});
            var Q30;
            Q30=makeQuery(id+"F13.imprint","IMPRINT",FACE,{"disambiguationData":[TD([[makeQuery(id+"F13.imprint","IMPRINT",EDGE,{"derivedFrom":sQuery(id+"F13.wireOp",EDGE,"E157")}),-1.0]])]});
            var Q31;
            Q31=makeQuery(id+"F13.imprint","IMPRINT",FACE,{"disambiguationData":[TD([[makeQuery(id+"F13.imprint","IMPRINT",EDGE,{"derivedFrom":sQuery(id+"F13.wireOp",EDGE,"E156")}),-1.0]])]});
            var Q32;
            Q32=makeQuery(id+"F13.imprint","IMPRINT",FACE,{"disambiguationData":[TD([[makeQuery(id+"F13.imprint","IMPRINT",EDGE,{"derivedFrom":sQuery(id+"F13.wireOp",EDGE,"E155")}),-1.0]])]});
            var Q33;
            Q33=makeQuery(id+"F13.imprint","IMPRINT",FACE,{"disambiguationData":[TD([[makeQuery(id+"F13.imprint","IMPRINT",EDGE,{"derivedFrom":sQuery(id+"F13.wireOp",EDGE,"E154")}),1.0]])]});
            var Q34;
            Q34=makeQuery(id+"F13.imprint","IMPRINT",FACE,{"disambiguationData":[TD([[makeQuery(id+"F13.imprint","IMPRINT",EDGE,{"derivedFrom":sQuery(id+"F13.wireOp",EDGE,"E153")}),-1.0]])]});
            var Q35;
            Q35=makeQuery(id+"F13.imprint","IMPRINT",FACE,{"disambiguationData":[TD([[makeQuery(id+"F13.imprint","IMPRINT",EDGE,{"derivedFrom":sQuery(id+"F13.wireOp",EDGE,"E152")}),-1.0]])]});
            var Q36;
            Q36=makeQuery(id+"F13.imprint","IMPRINT",FACE,{"disambiguationData":[TD([[makeQuery(id+"F13.imprint","IMPRINT",EDGE,{"derivedFrom":sQuery(id+"F13.wireOp",EDGE,"E151")}),1.0]])]});
            var Q37;
            Q37=makeQuery(id+"F13.imprint","IMPRINT",FACE,{"disambiguationData":[TD([[makeQuery(id+"F13.imprint","IMPRINT",EDGE,{"derivedFrom":sQuery(id+"F13.wireOp",EDGE,"E150")}),1.0]])]});
            var Q38;
            Q38=makeQuery(id+"F13.imprint","IMPRINT",FACE,{"disambiguationData":[TD([[makeQuery(id+"F13.imprint","IMPRINT",EDGE,{"derivedFrom":sQuery(id+"F13.wireOp",EDGE,"E149")}),-1.0]])]});
            var Q39;
            Q39=makeQuery(id+"F13.imprint","IMPRINT",FACE,{"disambiguationData":[TD([[makeQuery(id+"F13.imprint","IMPRINT",EDGE,{"derivedFrom":sQuery(id+"F13.wireOp",EDGE,"E148")}),-1.0]])]});
            extrude(context, id + "F17", {"entities" : qUnion([Q0, Q1, Q2, Q3, Q4, Q5, Q6, Q7, Q8, Q9, Q10, Q11, Q12, Q13, Q14, Q15, Q16, Q17, Q18, Q19, Q20, Q21, Q22, Q23, Q24, Q25, Q26, Q27, Q28, Q29, Q30, Q31, Q32, Q33, Q34, Q35, Q36, Q37, Q38, Q39]), "operationType" : NewBodyOperationType.ADD, "depth" : 6.5 * mm, "offsetDistance" : 25 * mm});
        }
        {
            var Q0;
            Q0=makeQuery(id+"F13.imprint","IMPRINT",FACE,{"disambiguationData":[TD([[makeQuery(id+"F13.imprint","IMPRINT",EDGE,{"derivedFrom":sQuery(id+"F13.wireOp",EDGE,"E173")}),1.0]])]});
            extrude(context, id + "F18", {"entities" : qUnion([Q0]), "operationType" : NewBodyOperationType.ADD, "depth" : 5 * mm, "offsetDistance" : 25 * mm});
        }
        {
            var Q0;
            Q0=qCreatedBy(makeId("Top.planeOp"),FACE);
            var sketch = newSketch(context, id + "F19", { "sketchPlane" : qUnion([Q0])});
            skCircle(sketch, "E174", {"center": v(0, 43.95) * mm, "radius": 4.28 * mm});
            skCircle(sketch, "E175", {"center": v(0, 43.95) * mm, "radius": 2.3 * mm});
            skLineSegment(sketch, "E176", {"start": v(-2.28, 43.7) * mm, "end": v(2.3, 43.95) * mm, "construction": true});
            skSolve(sketch);
        }
        {
            var Q0;
            Q0=makeQuery(id+"F19.imprint","IMPRINT",FACE,{"disambiguationData":[TD([[makeQuery(id+"F19.imprint","IMPRINT",EDGE,{"derivedFrom":sQuery(id+"F19.wireOp",EDGE,"E174")}),1.0]])]});
            extrude(context, id + "F20", {"entities" : qUnion([Q0]), "operationType" : NewBodyOperationType.ADD, "depth" : 4.25 * mm, "offsetDistance" : 25 * mm});
        }
    });
